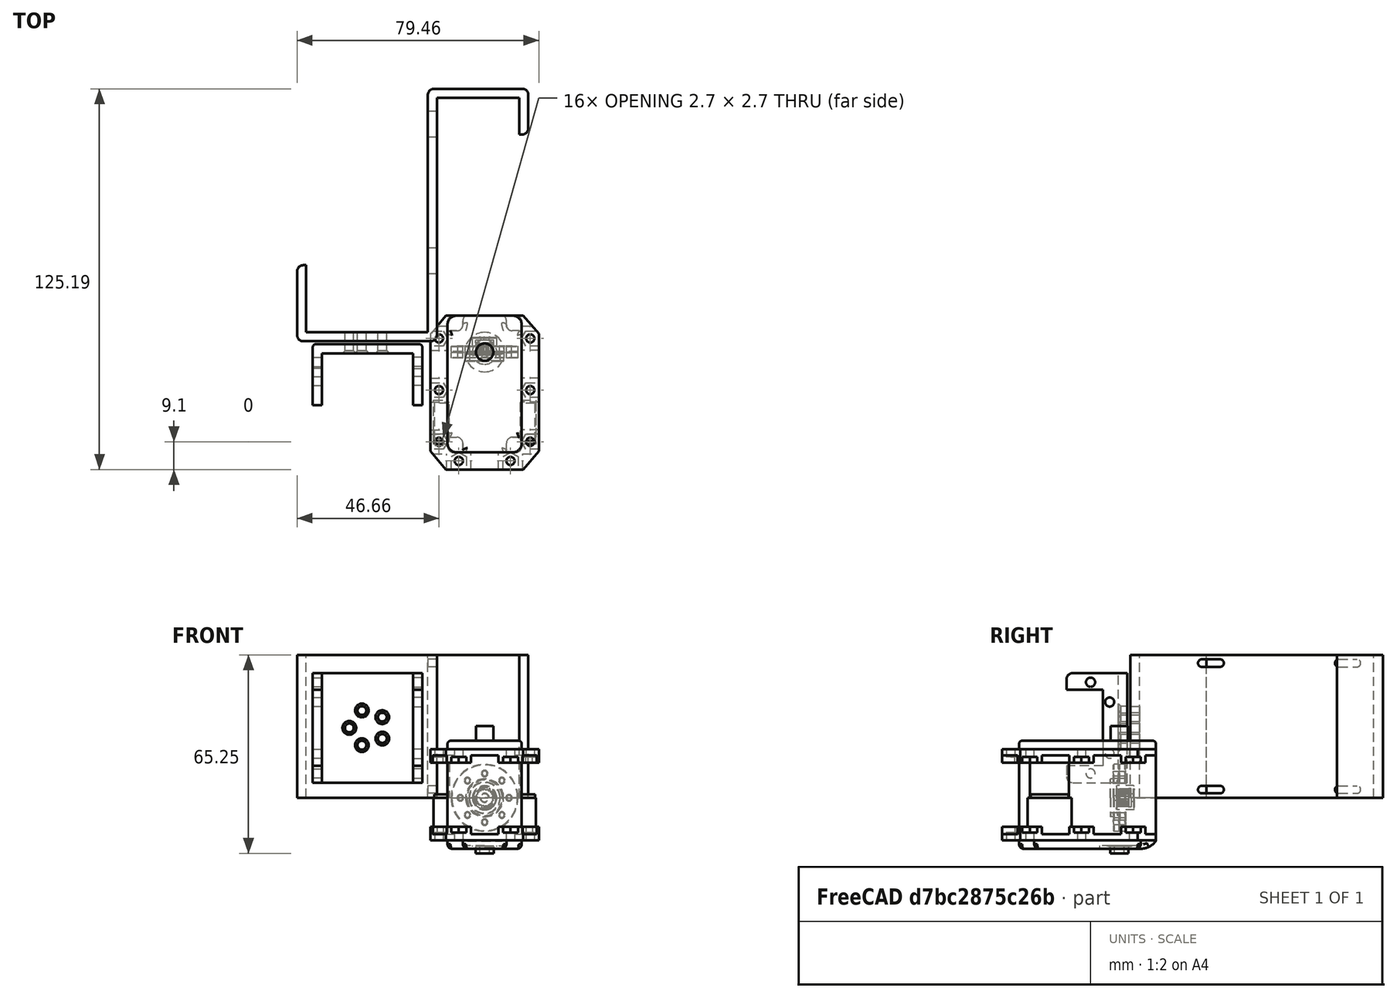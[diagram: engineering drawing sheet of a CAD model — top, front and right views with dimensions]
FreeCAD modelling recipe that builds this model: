
FCSTD DOCUMENT  (FreeCAD 1.1R20260414 (Git shallow))
Label: test2
License: All rights reserved
LicenseURL: https://en.wikipedia.org/wiki/All_rights_reserved
objects: App::Link×7, App::FeaturePython×7, App::Point×6, Sketcher::SketchObject×6, Part::Feature×5, PartDesign::Pad×3, PartDesign::Fillet×3, App::Part×3, PartDesign::Hole×2, PartDesign::Body×2, PartDesign::ShapeBinder×1, PartDesign::Mirrored×1, PartDesign::PolarPattern×1, Assembly::JointGroup×1, Assembly::AssemblyObject×1, PartDesign::Pocket×1, PartDesign::LinearPattern×1
note: 53 computed .brp shape members not serialized (recipe doc carries the construction recipe); baked Part::Feature solids carry a one-line shape summary decoded from their .brp
EXTERNAL_REF file=../test4/test4.FCStd obj=Body001
EXTERNAL_REF file=../test4/test4.FCStd obj=Body
EXTERNAL_REF file=../test4/test4.FCStd obj=ASM0001_ASM

FEATURE [App::Point] Origin001
  Role = Origin
FEATURE [Sketcher::SketchObject] Sketch
  ArcFitTolerance = 1e-06
  AttachmentSupport = -> [Origin]
  ExternalTypes = [0]
  FullyConstrained = true
  MakeInternals = false
  MapMode = 5
  _ExternalGeoVersion = 1
  sketch-geometry (12):
    g0: LineSegment StartX=-18.66 StartY=86.59 StartZ=0 EndX=-18.66 EndY=6.59 EndZ=0
    g1: LineSegment StartX=-61.66 StartY=3.59 StartZ=0 EndX=-61.66 EndY=28.59 EndZ=0
    g2: LineSegment StartX=-61.66 StartY=28.59 StartZ=0 EndX=-58.66 EndY=28.59 EndZ=0
    g3: LineSegment StartX=-58.66 StartY=28.59 StartZ=0 EndX=-58.66 EndY=6.59 EndZ=0
    g4: LineSegment StartX=-58.66 StartY=6.59 StartZ=0 EndX=-18.66 EndY=6.59 EndZ=0
    g5: LineSegment StartX=-15.66 StartY=83.59 StartZ=0 EndX=-15.66 EndY=3.59 EndZ=0
    g6: LineSegment StartX=-15.66 StartY=3.59 StartZ=0 EndX=-61.66 EndY=3.59 EndZ=0
    g7: LineSegment StartX=-15.66 StartY=83.59 StartZ=0 EndX=11.34 EndY=83.59 EndZ=0
    g8: LineSegment StartX=11.34 StartY=83.59 StartZ=0 EndX=11.34 EndY=71.59 EndZ=0
    g9: LineSegment StartX=11.34 StartY=71.59 StartZ=0 EndX=14.34 EndY=71.59 EndZ=0
    g10: LineSegment StartX=14.34 StartY=71.59 StartZ=0 EndX=14.34 EndY=86.59 EndZ=0
    g11: LineSegment StartX=14.34 StartY=86.59 StartZ=0 EndX=-18.66 EndY=86.59 EndZ=0
  constraints (36):
    c: Coincident(g1,g2)
    c: Coincident(g2,g3)
    c: Coincident(g3,g4)
    c: Coincident(g4,g0)
    c: Distance(g2,g2) = 3
    c: Vertical(g5)
    c: Coincident(g5,g6)
    c: Coincident(g6,g1)
    c: Perpendicular(g4,g3)
    c: Horizontal(g4)
    c: Horizontal(g6)
    c: Vertical(g1)
    c: Vertical(g0)
    c: Horizontal(g2)
    c: Distance(g6,g4) = 3
    c: Distance(g5,g0) = 3
    c: DistanceX(g4,g4) = 40
    c: Distance(g1,g1) = 25
    c: Distance(g-2,g5) = 15.66
    c: Distance(g-1,g6) = 3.59
    c: DistanceY(g0,g0) = 80
    c: Coincident(g5,g7)
    c: Horizontal(g7)
    c: Coincident(g7,g8)
    c: Vertical(g8)
    c: Coincident(g8,g9)
    c: Horizontal(g9)
    c: Coincident(g9,g10)
    c: Vertical(g10)
    c: Coincident(g10,g11)
    c: Coincident(g11,g0)
    c: Equal(g9,g2)
    c: Horizontal(g11)
    c: Distance(g11,g7) = 3
    c: Distance(g7,g7) = 27
    c: DistanceY(g10,g10) = 15
FEATURE [PartDesign::Pad] Pad
  Direction = (0,0,1)
  Length = 47
  Length2 = 10
  Profile = -> Sketch
  ReferenceAxis = -> Sketch [N_Axis]
  Refine = true
  SideType = 0
  Suppressed = false
  Type = 0
  Type2 = 0
FEATURE [Sketcher::SketchObject] Sketch001
  ArcFitTolerance = 1e-06
  ExternalTypes = [0]
  FullyConstrained = true
  MakeInternals = false
  MapMode = 5
  Placement = pos=(-15.66,0,0) rot=(0.57735,0.57735,0.57735;2.0944rad)
  _ExternalGeoVersion = 1
  sketch-geometry (8):
    g0: ArcOfCircle CenterX=72.09 CenterY=2.7 CenterZ=0 NormalX=0 NormalY=0 NormalZ=1 AngleXU=0 Radius=1.25 StartAngle=1.5708 EndAngle=4.71239
    g1: ArcOfCircle CenterX=78.09 CenterY=2.7 CenterZ=0 NormalX=0 NormalY=0 NormalZ=1 AngleXU=0 Radius=1.25 StartAngle=4.71239 EndAngle=7.85398
    g2: LineSegment StartX=72.09 StartY=3.95 StartZ=0 EndX=78.09 EndY=3.95 EndZ=0
    g3: LineSegment StartX=72.09 StartY=1.45 StartZ=0 EndX=78.09 EndY=1.45 EndZ=0
    g4: ArcOfCircle CenterX=27.09 CenterY=2.7 CenterZ=0 NormalX=0 NormalY=0 NormalZ=1 AngleXU=0 Radius=1.25 StartAngle=1.5708 EndAngle=4.71239
    g5: ArcOfCircle CenterX=33.09 CenterY=2.7 CenterZ=0 NormalX=0 NormalY=0 NormalZ=1 AngleXU=0 Radius=1.25 StartAngle=4.71239 EndAngle=7.85398
    g6: LineSegment StartX=27.09 StartY=3.95 StartZ=0 EndX=33.09 EndY=3.95 EndZ=0
    g7: LineSegment StartX=27.09 StartY=1.45 StartZ=0 EndX=33.09 EndY=1.45 EndZ=0
  constraints (20):
    c: Tangent(g0,g2) = 1.5708
    c: Tangent(g0,g3) = -1.5708
    c: Tangent(g1,g2) = 1.5708
    c: Tangent(g1,g3) = -1.5708
    c: Equal(g0,g1)
    c: Distance(g0,g1) = 6
    c: Radius(g0) = 1.25
    c: Horizontal(g2)
    c: Distance(g1,g-1) = 2.7
    c: DistanceX(g-1,g1) = 78.09
    c: Tangent(g4,g6) = 1.5708
    c: Tangent(g4,g7) = -1.5708
    c: Tangent(g5,g6) = 1.5708
    c: Tangent(g5,g7) = -1.5708
    c: Equal(g4,g5)
    c: Distance(g4,g5) = 6
    c: Radius(g4) = 1.25
    c: Horizontal(g6)
    c: DistanceX(g5,g1) = 45
    c: Distance(g5,g-1) = 2.7
FEATURE [App::Point] Origin003
  Role = Origin
FEATURE [App::Point] Origin005  label="Origin006"
  Role = Origin
FEATURE [App::Link] Body003
  LinkPlacement = pos=(-38.5,-38.01,23) rot=(-0.707107,0,0.707107;3.14159rad)
  LinkedObject = -> Body001
  Placement = pos=(-38.5,-38.01,23) rot=(-0.707107,0,0.707107;3.14159rad)
FEATURE [PartDesign::ShapeBinder] CopyPart__Feature
  TraceSupport = false
FEATURE [Sketcher::SketchObject] Sketch002
  ArcFitTolerance = 1e-06
  AttachmentSupport = -> [CopyPart__Feature]
  ExternalTypes = [0]
  FullyConstrained = true
  MakeInternals = false
  MapMode = 5
  Placement = pos=(0,-38.6,0) rot=(1,0,0;1.5708rad)
  _ExternalGeoVersion = 1
  sketch-geometry (5):
    g0: LineSegment StartX=-18 StartY=-15 StartZ=0 EndX=18 EndY=-15 EndZ=0
    g1: LineSegment StartX=18 StartY=-15 StartZ=0 EndX=18 EndY=15 EndZ=0
    g2: LineSegment StartX=18 StartY=15 StartZ=0 EndX=-18 EndY=15 EndZ=0
    g3: LineSegment StartX=-18 StartY=15 StartZ=0 EndX=-18 EndY=-15 EndZ=0
    g4: GeomPoint [constr] X=0 Y=0 Z=0
  constraints (12):
    c: Coincident(g0,g1)
    c: Coincident(g1,g2)
    c: Coincident(g2,g3)
    c: Coincident(g3,g0)
    c: Horizontal(g0)
    c: Horizontal(g2)
    c: Vertical(g1)
    c: Vertical(g3)
    c: Symmetric(g2,g0,g4)
    c: Distance(g1,g3) = 36
    c: Distance(g0,g2) = 30
    c: Coincident(g4,g-1)
FEATURE [PartDesign::Pad] Pad001
  Direction = (0,-1,2e-16)
  Length = 3
  Length2 = 10
  Profile = -> Sketch002
  ReferenceAxis = -> Sketch002 [N_Axis]
  Refine = true
  SideType = 0
  Suppressed = false
  Type = 0
  Type2 = 0
FEATURE [Sketcher::SketchObject] Sketch003
  ArcFitTolerance = 1e-06
  AttachmentSupport = -> [Pad001]
  ExternalTypes = [0]
  FullyConstrained = true
  MakeInternals = false
  MapMode = 5
  Placement = pos=(0,3.3e-15,15) rot=(0,0,1;0rad)
  _ExternalGeoVersion = 1
  sketch-geometry (12):
    g0: LineSegment StartX=-18 StartY=-21.6 StartZ=0 EndX=-12.5 EndY=-21.6 EndZ=0
    g1: LineSegment StartX=-12.5 StartY=-21.6 StartZ=0 EndX=-12.5 EndY=-33.6 EndZ=0
    g2: LineSegment StartX=-12.5 StartY=-33.6 StartZ=0 EndX=12.5 EndY=-33.6 EndZ=0
    g3: LineSegment StartX=12.5 StartY=-33.6 StartZ=0 EndX=12.5 EndY=-21.6 EndZ=0
    g4: LineSegment StartX=12.5 StartY=-21.6 StartZ=0 EndX=18 EndY=-21.6 EndZ=0
    g5: LineSegment StartX=18 StartY=-21.6 StartZ=0 EndX=18 EndY=-41.6 EndZ=0
    g6: LineSegment StartX=18 StartY=-41.6 StartZ=0 EndX=-18 EndY=-41.6 EndZ=0
    g7: LineSegment StartX=-18 StartY=-41.6 StartZ=0 EndX=-18 EndY=-21.6 EndZ=0
    g8: Circle CenterX=-15 CenterY=-29.5 CenterZ=0 NormalX=0 NormalY=0 NormalZ=1 AngleXU=0 Radius=1.5
    g9: Circle CenterX=-8.5 CenterY=-35.8 CenterZ=0 NormalX=0 NormalY=0 NormalZ=1 AngleXU=0 Radius=1.5
    g10: Circle CenterX=8.5 CenterY=-35.8 CenterZ=0 NormalX=0 NormalY=0 NormalZ=1 AngleXU=0 Radius=1.5
    g11: Circle CenterX=15 CenterY=-29.5 CenterZ=0 NormalX=0 NormalY=0 NormalZ=1 AngleXU=0 Radius=1.5
  constraints (36):
    c: Horizontal(g0)
    c: Coincident(g0,g1)
    c: Vertical(g1)
    c: Coincident(g1,g2)
    c: Horizontal(g2)
    c: Coincident(g2,g3)
    c: Vertical(g3)
    c: Coincident(g3,g4)
    c: Horizontal(g4)
    c: Coincident(g4,g5)
    c: Vertical(g5)
    c: Coincident(g5,g6)
    c: Horizontal(g6)
    c: Coincident(g6,g7)
    c: Coincident(g7,g0)
    c: Vertical(g7)
    c: DistanceX(g6,g6) = 36
    c: DistanceY(g7,g7) = 20
    c: Distance(g3,g1) = 25
    c: Equal(g0,g4)
    c: Equal(g3,g1)
    c: Distance(g-1,g6) = 41.6
    c: Distance(g-2,g7) = 18
    c: Distance(g6,g2) = 8
    c: Diameter(g8) = 3
    c: Equal(g8,g9)
    c: Equal(g9,g10)
    c: Equal(g10,g11)
    c: Distance(g8,g7) = 3
    c: Distance(g9,g6) = 5.8
    c: Distance(g9,g7) = 9.5
    c: Distance(g10,g5) = 9.5
    c: Distance(g10,g6) = 5.8
    c: Distance(g11,g5) = 3
    c: Distance(g8,g0) = 7.9
    c: Distance(g11,g4) = 7.9
FEATURE [PartDesign::Pad] Pad002
  BaseFeature = -> Pad001
  Direction = (0,0,1)
  Length = 3
  Length2 = 10
  Profile = -> Sketch003
  ReferenceAxis = -> Sketch003 [N_Axis]
  Refine = true
  SideType = 0
  Suppressed = false
  Type = 0
  Type2 = 0
FEATURE [PartDesign::Mirrored] Mirrored
  BaseFeature = -> Pad002
  MirrorPlane = -> XY_Plane001
  Originals = -> [Pad002]
  Refine = true
  Suppressed = false
  TransformMode = 0
FEATURE [PartDesign::Fillet] Fillet001
  Base = -> Mirrored [Edge60,Edge47,Edge36,Edge27]
  BaseFeature = -> Mirrored
  Radius = 2
  Refine = true
  SupportTransform = false
  Suppressed = false
  UseAllEdges = false
FEATURE [PartDesign::Fillet] Fillet002
  Base = -> Fillet001 [Edge51,Edge56]
  BaseFeature = -> Fillet001
  Radius = 1
  Refine = true
  SupportTransform = false
  Suppressed = false
  UseAllEdges = false
FEATURE [Sketcher::SketchObject] Sketch004
  ArcFitTolerance = 1e-06
  AttachmentSupport = -> [Fillet002]
  ExternalTypes = [0]
  FullyConstrained = true
  MakeInternals = false
  MapMode = 5
  Placement = pos=(0,-38.6,0) rot=(0,0.707107,0.707107;3.14159rad)
  _ExternalGeoVersion = 1
  sketch-geometry (1):
    g0: Circle CenterX=0 CenterY=6 CenterZ=0 NormalX=0 NormalY=0 NormalZ=1 AngleXU=0 Radius=1.25
  constraints (3):
    c: Diameter(g0) = 2.5
    c: PointOnObject(g0,g-2)
    c: Distance(g0,g-1) = 6
FEATURE [PartDesign::Hole] Hole
  BaseFeature = -> Fillet002
  BaseProfileType = 7
  CustomThreadClearance = 0
  Depth = 5
  DepthType = 0
  Diameter = 2.9
  DrillForDepth = false
  DrillPoint = 1
  DrillPointAngle = 118
  HoleCutCountersinkAngle = 90
  HoleCutCustomValues = false
  HoleCutDepth = 2.65
  HoleCutDiameter = 5.3
  HoleCutType = 7
  ModelThread = false
  Profile = -> Sketch004
  Refine = true
  Suppressed = false
  Tapered = false
  TaperedAngle = 90
  ThreadClass = 0
  ThreadDepth = 5
  ThreadDepthType = 0
  ThreadDiameter = 2.5
  ThreadDirection = 0
  ThreadFit = 0
  ThreadSize = 8
  ThreadType = 1
  Threaded = false
  UseCustomThreadClearance = false
FEATURE [PartDesign::PolarPattern] PolarPattern
  Angle = 360
  Axis = -> Sketch004 [N_Axis]
  BaseFeature = -> Hole
  Mode = 0
  Occurrences = 5
  Offset = 120
  Originals = -> [Hole]
  Refine = true
  SpacingPattern = [0]
  Spacings = [-1,-1,-1,-1]
  Suppressed = false
  TransformMode = 0
FEATURE [PartDesign::Body] Body001
  AllowCompound = true
  Group = -> [CopyPart__Feature,Sketch002,Pad001,Sketch003,Pad002,Mirrored,Fillet001,Fillet002,Sketch004,Hole,PolarPattern]
  Origin = -> Origin002
  Placement = pos=(-38.5,-39,23) rot=(0.707107,0,-0.707107;3.14159rad)
  Tip = -> PolarPattern
FEATURE [App::Link] Body004
  LinkedObject = -> Body
FEATURE [App::FeaturePython] GroundedJoint  label="GroundedJoint001"  # Assembly grounded joint (typed FeaturePython)
  ObjectToGround = -> Body004
FEATURE [App::FeaturePython] Joint  label="Fixed015"  # Assembly joint (typed FeaturePython)
  Angle = 0
  AngleMax = 0
  AngleMin = 0
  Detach1 = false
  Detach2 = false
  Distance = 0
  Distance2 = 0
  EnableAngleMax = false
  EnableAngleMin = false
  EnableLengthMax = false
  EnableLengthMin = false
  JointType = 0 (Fixed)
  LengthMax = 0
  LengthMin = 0
  Offset2 = pos=(0,0,0) rot=(0,0,1;1.5708rad)
  Placement1 = pos=(-44.5,3.59,23) rot=(0,-0.707107,0.707107;3.14159rad)
  Placement2 = pos=(3.6e-15,-41.6,6) rot=(0.57735,-0.57735,0.57735;2.0944rad)
  Reference1 = -> Body004 [Edge68,Edge68]
  Reference2 = -> Body003 [Edge32,Edge32]
  Suppressed = false
FEATURE [App::Point] Origin006  label="Origin008"
  Role = Origin
FEATURE [Part::Feature] Part__Feature  label="DC07_00A_DUMMY_NONE"
  Placement = pos=(0,0,1) rot=(0,0,1;0rad)
  shape: bbox 35.6 x 51.12 x 41.85 mm, 333 faces (baked)
FEATURE [App::Point] Origin008  label="Origin010"
  Role = Origin
FEATURE [Part::Feature] Part__Feature001  label="SOLID001"
  shape: bbox 22 x 3.05 x 22 mm, 56 faces (baked)
FEATURE [Part::Feature] Part__Feature002  label="COMPOUND001"
  shape: bbox 18 x 1.95 x 18 mm, 16 faces, 0 solids (baked)
FEATURE [App::Part] HN07_I_02
  Group = -> [Part__Feature001,Part__Feature002]
  Origin = -> Origin009
  Placement = pos=(2e-16,0,-19.15) rot=(-0.672416,0.523382,-0.523382;1.95765rad)
FEATURE [App::Point] Origin010  label="Origin012"
  Role = Origin
FEATURE [Part::Feature] Part__Feature003  label="SOLID"
  shape: bbox 22 x 5.851 x 22 mm, 149 faces (baked)
FEATURE [Part::Feature] Part__Feature004  label="COMPOUND"
  shape: bbox 18 x 1.95 x 18 mm, 16 faces, 0 solids (baked)
FEATURE [App::Part] HN07_N_02
  Group = -> [Part__Feature003,Part__Feature004]
  Origin = -> Origin011
  Placement = pos=(0,0,19.3) rot=(0.57735,0.57735,0.57735;2.0944rad)
FEATURE [App::Part] Unnamed  label="mx28"
  Group = -> [Part__Feature,HN07_I_02,HN07_N_02]
  Origin = -> Origin007
FEATURE [App::Link] mx28  label="mx001"
  LinkPlacement = pos=(-37.5,-38.01,23) rot=(-0.707107,0,0.707107;3.14159rad)
  LinkedObject = -> Unnamed
  Placement = pos=(-37.5,-38.01,23) rot=(-0.707107,0,0.707107;3.14159rad)
FEATURE [App::FeaturePython] Joint001  label="Fixed017"  # Assembly joint (typed FeaturePython)
  Angle = 0
  AngleMax = 0
  AngleMin = 0
  Detach1 = false
  Detach2 = false
  Distance = 0
  Distance2 = 0
  EnableAngleMax = false
  EnableAngleMin = false
  EnableLengthMax = false
  EnableLengthMin = false
  JointType = 0 (Fixed)
  LengthMax = 0
  LengthMin = 0
  Offset2 = pos=(0,0,-1.5) rot=(0,0,1;0rad)
  Placement1 = pos=(8.5,-35.8,15) rot=(1,0,0;3.14159rad)
  Placement2 = pos=(8.5,-35.8,15) rot=(0,0,1;0rad)
  Reference1 = -> mx28 [Part__Feature.Edge697,Part__Feature.Edge697]
  Reference2 = -> Body003 [Face21,Face21]
  Suppressed = false
FEATURE [App::Link] Body005
  LinkPlacement = pos=(-30.115,-30.5656,31.2547) rot=(-0.706989,-0.018235,0.706989;3.10513rad)
  LinkedObject = -> <external ../test4/test4.FCStd>#Body001
  Placement = pos=(-30.115,-30.5656,31.2547) rot=(-0.706989,-0.018235,0.706989;3.10513rad)
FEATURE [App::FeaturePython] Joint002  label="Revolute018"  # Assembly joint (typed FeaturePython)
  Angle = 0
  AngleMax = 0
  AngleMin = 0
  Detach1 = false
  Detach2 = false
  Distance = 0
  Distance2 = 0
  EnableAngleMax = false
  EnableAngleMin = false
  EnableLengthMax = false
  EnableLengthMin = false
  JointType = 1 (Revolute)
  LengthMax = 0
  LengthMin = 0
  Offset2 = pos=(0,0,2.5) rot=(0,0,1;0rad)
  Placement1 = pos=(0,4.65,0) rot=(0,-0.707107,0.707107;3.14159rad)
  Placement2 = pos=(7.86,7.86,31.335) rot=(0,0,1;0rad)
  Reference1 = -> mx28 [HN07_N_02.Part__Feature003.Face53,HN07_N_02.Part__Feature003.Edge4]
  Reference2 = -> Body005 [Edge45,Edge45]
  Suppressed = false
FEATURE [App::Link] Body006
  LinkPlacement = pos=(-16.8936,-106.981,69.1522) rot=(0.706989,0.018235,-0.706989;3.17806rad)
  LinkedObject = -> <external ../test4/test4.FCStd>#Body
  Placement = pos=(-16.8936,-106.981,69.1522) rot=(0.706989,0.018235,-0.706989;3.17806rad)
FEATURE [App::Link] ASM0001_ASM
  LinkPlacement = pos=(-16.5936,-105.125,33.2001) rot=(0.706989,-0.018235,0.706989;3.17806rad)
  LinkedObject = -> <external ../test4/test4.FCStd>#ASM0001_ASM
  Placement = pos=(-16.5936,-105.125,33.2001) rot=(0.706989,-0.018235,0.706989;3.17806rad)
FEATURE [App::Link] ASM0001_ASM001
  LinkPlacement = pos=(-16.5936,-106.981,69.1522) rot=(0.706989,-0.018235,0.706989;3.17806rad)
  LinkedObject = -> <external ../test4/test4.FCStd>#ASM0001_ASM
  Placement = pos=(-16.5936,-106.981,69.1522) rot=(0.706989,-0.018235,0.706989;3.17806rad)
FEATURE [App::FeaturePython] Joint003  label="Fixed021"  # Assembly joint (typed FeaturePython)
  Angle = 0
  AngleMax = 0
  AngleMin = 0
  Detach1 = false
  Detach2 = false
  Distance = 0
  Distance2 = 0
  EnableAngleMax = false
  EnableAngleMin = false
  EnableLengthMax = false
  EnableLengthMin = false
  JointType = 0 (Fixed)
  LengthMax = 0
  LengthMin = 0
  Placement1 = pos=(10.2136,32.86,3.77861) rot=(0.57735,0.57735,0.57735;4.18879rad)
  Placement2 = pos=(52,-41.5,17) rot=(0.57735,0.57735,0.57735;4.18879rad)
  Reference1 = -> Body005 [Face9,Vertex51]
  Reference2 = -> Body006 [Face28,Edge6]
  Suppressed = false
FEATURE [App::FeaturePython] Joint004  label="Fixed022"  # Assembly joint (typed FeaturePython)
  Angle = 0
  AngleMax = 0
  AngleMin = 0
  Detach1 = false
  Detach2 = false
  Distance = 0
  Distance2 = 0
  EnableAngleMax = false
  EnableAngleMin = false
  EnableLengthMax = false
  EnableLengthMin = false
  JointType = 0 (Fixed)
  LengthMax = 0
  LengthMin = 0
  Offset2 = pos=(0,0,-0.2) rot=(0,0,-1;1.5708rad)
  Placement1 = pos=(13.5,-30.5,16) rot=(0,0,1;1.5708rad)
  Placement2 = pos=(-13.5,-30.5,-16.3) rot=(-0.707107,-0.707107,0;3.14159rad)
  Reference1 = -> ASM0001_ASM001 [ASM0002_ASM.Part__Feature.Edge804,ASM0002_ASM.Part__Feature.Edge804]
  Reference2 = -> Body006 [Edge110,Edge110]
  Suppressed = false
FEATURE [App::FeaturePython] Joint005  label="Fixed023"  # Assembly joint (typed FeaturePython)
  Angle = 0
  AngleMax = 0
  AngleMin = 0
  Detach1 = false
  Detach2 = false
  Distance = 0
  Distance2 = 0
  EnableAngleMax = false
  EnableAngleMin = false
  EnableLengthMax = false
  EnableLengthMin = false
  JointType = 0 (Fixed)
  LengthMax = 0
  LengthMin = 0
  Offset2 = pos=(0,0,-0.2) rot=(0,0,1;1.5708rad)
  Placement1 = pos=(-13.5,-30.5,16) rot=(0,0,-1;1.5708rad)
  Placement2 = pos=(49.5,-30.5,-16.3) rot=(-0.707107,0.707107,0;3.14159rad)
  Reference1 = -> ASM0001_ASM [ASM0002_ASM.Part__Feature.Edge809,ASM0002_ASM.Part__Feature.Edge809]
  Reference2 = -> Body006 [Edge104,Edge104]
  Suppressed = false
FEATURE [Assembly::JointGroup] Joints
  Group = -> [GroundedJoint,Joint,Joint001,Joint002,Joint003,Joint004,Joint005]
FEATURE [Assembly::AssemblyObject] Assembly
  Group = -> [Joints,Body003,Body004,GroundedJoint,Joint,mx28,Joint001,Body005,Joint002,Body006,ASM0001_ASM,ASM0001_ASM001,Joint003,Joint004,Joint005]
  Origin = -> Origin004
  Type = Assembly
FEATURE [PartDesign::Fillet] Fillet
  Base = -> Pad [Edge26,Edge29,Edge32,Edge8,Edge11,Edge14]
  BaseFeature = -> Pad
  Radius = 2
  Refine = true
  SupportTransform = false
  Suppressed = false
  UseAllEdges = false
FEATURE [PartDesign::Pocket] Pocket
  BaseFeature = -> Fillet
  Direction = (-1,0,0)
  Length = 5
  Length2 = 5
  Profile = -> Sketch001
  ReferenceAxis = -> Sketch001 [N_Axis]
  Refine = true
  SideType = 0
  Suppressed = false
  Type = 0
  Type2 = 0
FEATURE [PartDesign::LinearPattern] LinearPattern
  BaseFeature = -> Pocket
  Direction = -> Sketch001 [V_Axis]
  Direction2 = -> Sketch001 [V_Axis]
  Length = 41.6
  Length2 = 100
  Mode = 0
  Mode2 = 0
  Occurrences = 2
  Occurrences2 = 1
  Offset = 41.6
  Offset2 = 100
  Originals = -> [Pocket]
  Refine = true
  Reversed2 = false
  SpacingPattern = [0]
  SpacingPattern2 = [0]
  Spacings = [-1]
  Suppressed = false
  TransformMode = 0
FEATURE [Sketcher::SketchObject] Sketch005
  ArcFitTolerance = 1e-06
  AttachmentSupport = -> [LinearPattern]
  ExternalTypes = [0]
  FullyConstrained = true
  MakeInternals = false
  Placement = pos=(0,3.59,0) rot=(1,0,0;1.5708rad)
  _ExternalGeoVersion = 1
  sketch-geometry (5):
    g0: Circle CenterX=-40.37 CenterY=17.3 CenterZ=0 NormalX=0 NormalY=0 NormalZ=1 AngleXU=0 Radius=1.25
    g1: Circle CenterX=-44.5 CenterY=23 CenterZ=0 NormalX=0 NormalY=0 NormalZ=1 AngleXU=0 Radius=1.25
    g2: Circle CenterX=-40.36 CenterY=28.7 CenterZ=0 NormalX=0 NormalY=0 NormalZ=1 AngleXU=0 Radius=1.25
    g3: Circle CenterX=-33.65 CenterY=26.55 CenterZ=0 NormalX=0 NormalY=0 NormalZ=1 AngleXU=0 Radius=1.25
    g4: Circle CenterX=-33.65 CenterY=19.5 CenterZ=0 NormalX=0 NormalY=0 NormalZ=1 AngleXU=0 Radius=1.25
  constraints (15):
    c: Diameter(g0) = 2.5
    c: Distance(g0,g-1) = 17.3
    c: Distance(g0,g-2) = 40.37
    c: Equal(g1,g0)
    c: Distance(g1,g-1) = 23
    c: DistanceX(g1,g-1) = 44.5
    c: Equal(g2,g1)
    c: Equal(g3,g2)
    c: Equal(g4,g3)
    c: Distance(g2,g-1) = 28.7
    c: Distance(g2,g-2) = 40.36
    c: Distance(g3,g-2) = 33.65
    c: Distance(g3,g-1) = 26.55
    c: Distance(g4,g-2) = 33.65
    c: DistanceY(g-1,g4) = 19.5
FEATURE [PartDesign::Hole] Hole001
  BaseFeature = -> LinearPattern
  BaseProfileType = 7
  CustomThreadClearance = 0
  Depth = 5
  DepthType = 0
  Diameter = 2.9
  DrillForDepth = false
  DrillPoint = 1
  DrillPointAngle = 118
  HoleCutCountersinkAngle = 90
  HoleCutCustomValues = false
  HoleCutDepth = 0
  HoleCutDiameter = 5.3
  HoleCutType = 0
  ModelThread = false
  Profile = -> Sketch005
  Refine = true
  Suppressed = false
  Tapered = false
  TaperedAngle = 90
  ThreadClass = 0
  ThreadDepth = 5
  ThreadDepthType = 0
  ThreadDiameter = 2.5
  ThreadDirection = 0
  ThreadFit = 0
  ThreadSize = 8
  ThreadType = 1
  Threaded = false
  UseCustomThreadClearance = false
FEATURE [PartDesign::Body] Body
  AllowCompound = true
  Group = -> [Sketch,Pad,Fillet,Sketch001,Pocket,LinearPattern,Sketch005,Hole001]
  Origin = -> Origin
  Tip = -> Hole001

RESOLVED EXTERNAL PARTS (link-assembly join: the EXTERNAL_REF files above that resolve inside this repo's crawl, each included once):
---- part ../test4/test4.FCStd = doc fcstd_3a8577a0ba73 ----
FCSTD DOCUMENT  (FreeCAD 1.1R20260414 (Git shallow))
Label: test4
License: All rights reserved
LicenseURL: https://en.wikipedia.org/wiki/All_rights_reserved
objects: Sketcher::SketchObject×26, Part::Feature×23, PartDesign::Pad×16, PartDesign::Hole×10, App::Point×8, PartDesign::Fillet×7, PartDesign::PolarPattern×5, App::Part×4, PartDesign::ShapeBinder×4, PartDesign::Body×4, PartDesign::Mirrored×3
note: 198 computed .brp shape members not serialized (recipe doc carries the construction recipe); baked Part::Feature solids carry a one-line shape summary decoded from their .brp

FEATURE [Part::Feature] Part__Feature  label="PRT0001"
  shape: bbox 32 x 50.5 x 38 mm, 671 faces (baked)
FEATURE [Part::Feature] Part__Feature001  label="PRT0002"
  Placement = pos=(0,0,-2) rot=(0,0,1;3.14159rad)
  shape: bbox 7.033 x 7.036 x 5.513 mm, 32 faces (baked)
FEATURE [Part::Feature] Part__Feature002  label="PRT0003"
  Placement = pos=(9.5,8.5,14.5) rot=(0,0.707107,0.707107;3.14159rad)
  shape: bbox 4.1 x 4.088 x 30.71 mm, 30 faces (baked)
FEATURE [Part::Feature] Part__Feature003  label="PRT0004"
  Placement = pos=(-9.5,8.5,14.5) rot=(0,0.707107,0.707107;3.14159rad)
  shape: bbox 4.1 x 4.088 x 30.71 mm, 30 faces (baked)
FEATURE [Part::Feature] Part__Feature004  label="PRT0005"
  Placement = pos=(10.5,-33,14.5) rot=(0,0.707107,0.707107;3.14159rad)
  shape: bbox 4.1 x 4.088 x 30.71 mm, 30 faces (baked)
FEATURE [Part::Feature] Part__Feature005  label="PRT0006"
  Placement = pos=(-10.5,-33,14.5) rot=(0,0.707107,0.707107;3.14159rad)
  shape: bbox 4.1 x 4.088 x 30.71 mm, 30 faces (baked)
FEATURE [Part::Feature] Part__Feature006  label="PRT0007"
  Placement = pos=(5.05,-15.19,-9.75) rot=(-1,0,0;1.5708rad)
  shape: bbox 9.902 x 4.902 x 9.405 mm, 93 faces (baked)
FEATURE [Part::Feature] Part__Feature007  label="PRT0008"
  Placement = pos=(-4.95,-15.19,-9.75) rot=(-1,0,0;1.5708rad)
  shape: bbox 9.902 x 4.902 x 9.405 mm, 93 faces (baked)
FEATURE [Part::Feature] Part__Feature008  label="PRT0009"
  Placement = pos=(0,0,-18.4) rot=(0,0.707107,0.707107;3.14159rad)
  shape: bbox 4.984 x 4.984 x 7 mm, 133 faces (baked)
FEATURE [Part::Feature] Part__Feature009  label="PRT0010"
  Placement = pos=(0,0,19.16) rot=(0,0,1;1.5708rad)
  shape: bbox 22 x 22 x 6.702 mm, 170 faces (baked)
FEATURE [Part::Feature] Part__Feature010  label="PRT0011"
  Placement = pos=(0,0,19.48) rot=(0,0.707107,0.707107;3.14159rad)
  shape: bbox 7.815 x 6.706 x 9.6 mm, 27 faces (baked)
FEATURE [App::Part] ASM0002_ASM
  Group = -> [Part__Feature,Part__Feature001,Part__Feature002,Part__Feature003,Part__Feature004,Part__Feature005,Part__Feature006,Part__Feature007,Part__Feature008,Part__Feature009,Part__Feature010]
  Origin = -> Origin
FEATURE [App::Point] Origin001
  Role = Origin
FEATURE [App::Part] ASM0001_ASM
  Group = -> [ASM0002_ASM]
  Origin = -> Origin002
  Placement = pos=(-5,-22,0) rot=(0,0,1;4.71239rad)
FEATURE [App::Point] Origin003
  Role = Origin
FEATURE [App::Point] Origin005  label="Origin006"
  Role = Origin
FEATURE [PartDesign::ShapeBinder] CopyPart__Feature
  TraceSupport = false
FEATURE [Sketcher::SketchObject] Sketch
  ArcFitTolerance = 1e-06
  AttachmentSupport = -> [CopyPart__Feature]
  ExternalTypes = [0]
  FullyConstrained = true
  MakeInternals = false
  MapMode = 5
  Placement = pos=(0,-38.5,0) rot=(1,0,0;1.5708rad)
  _ExternalGeoVersion = 1
  sketch-geometry (5):
    g0: LineSegment StartX=-44.42 StartY=-19 StartZ=0 EndX=69.58 EndY=-19 EndZ=0
    g1: LineSegment StartX=69.58 StartY=-19 StartZ=0 EndX=69.58 EndY=19 EndZ=0
    g2: LineSegment StartX=69.58 StartY=19 StartZ=0 EndX=-44.42 EndY=19 EndZ=0
    g3: LineSegment StartX=-44.42 StartY=19 StartZ=0 EndX=-44.42 EndY=-19 EndZ=0
    g4: GeomPoint [constr] X=12.58 Y=0 Z=0
  constraints (13):
    c: Coincident(g0,g1)
    c: Coincident(g1,g2)
    c: Coincident(g2,g3)
    c: Coincident(g3,g0)
    c: Horizontal(g0)
    c: Horizontal(g2)
    c: Vertical(g1)
    c: Vertical(g3)
    c: Symmetric(g2,g0,g4)
    c: Distance(g1,g3) = 114
    c: Distance(g0,g2) = 38
    c: PointOnObject(g4,g-1)
    c: Distance(g-2,g3) = 44.42
FEATURE [PartDesign::Pad] Pad
  Direction = (0,-1,0)
  Length = 5
  Length2 = 10
  Profile = -> Sketch
  ReferenceAxis = -> Sketch [N_Axis]
  Refine = true
  SideType = 0
  Suppressed = false
  Type = 0
  Type2 = 0
FEATURE [Sketcher::SketchObject] Sketch001
  ArcFitTolerance = 1e-06
  AttachmentSupport = -> [Pad]
  ExternalTypes = [0]
  FullyConstrained = true
  MakeInternals = false
  MapMode = 5
  Placement = pos=(0,-38.5,1.44e-14) rot=(0,0.707107,0.707107;3.14159rad)
  _ExternalGeoVersion = 1
  sketch-geometry (4):
    g0: LineSegment StartX=44.42 StartY=19 StartZ=0 EndX=-69.58 EndY=19 EndZ=0
    g1: LineSegment StartX=-69.58 StartY=19 StartZ=0 EndX=-69.58 EndY=15.5 EndZ=0
    g2: LineSegment StartX=-69.58 StartY=15.5 StartZ=0 EndX=44.42 EndY=15.5 EndZ=0
    g3: LineSegment StartX=44.42 StartY=15.5 StartZ=0 EndX=44.42 EndY=19 EndZ=0
  constraints (12):
    c: Coincident(g0,g1)
    c: Coincident(g1,g2)
    c: Coincident(g2,g3)
    c: Coincident(g3,g0)
    c: Horizontal(g0)
    c: Horizontal(g2)
    c: Vertical(g1)
    c: Vertical(g3)
    c: Distance(g-2,g3) = 44.42
    c: Distance(g2,g2) = 114
    c: Distance(g-1,g0) = 19
    c: Distance(g1,g1) = 3.5
FEATURE [PartDesign::Pad] Pad001
  BaseFeature = -> Pad
  Direction = (0,1,-2e-16)
  Length = 5
  Length2 = 10
  Profile = -> Sketch001
  ReferenceAxis = -> Sketch001 [N_Axis]
  Refine = true
  SideType = 0
  Suppressed = false
  Type = 0
  Type2 = 0
FEATURE [App::Point] Origin007  label="Origin009"
  Role = Origin
FEATURE [App::Point] Origin009  label="Origin011"
  Role = Origin
FEATURE [Part::Feature] Part__Feature011  label="PRT0012"
  shape: bbox 32 x 50.5 x 38 mm, 671 faces (baked)
FEATURE [Part::Feature] Part__Feature012  label="PRT0013"
  Placement = pos=(0,0,-2) rot=(0,0,1;3.14159rad)
  shape: bbox 7.033 x 7.036 x 5.513 mm, 32 faces (baked)
FEATURE [Part::Feature] Part__Feature013  label="PRT0014"
  Placement = pos=(9.5,8.5,14.5) rot=(0,0.707107,0.707107;3.14159rad)
  shape: bbox 4.1 x 4.088 x 30.71 mm, 30 faces (baked)
FEATURE [Part::Feature] Part__Feature014  label="PRT0015"
  Placement = pos=(-9.5,8.5,14.5) rot=(0,0.707107,0.707107;3.14159rad)
  shape: bbox 4.1 x 4.088 x 30.71 mm, 30 faces (baked)
FEATURE [Part::Feature] Part__Feature015  label="PRT0016"
  Placement = pos=(10.5,-33,14.5) rot=(0,0.707107,0.707107;3.14159rad)
  shape: bbox 4.1 x 4.088 x 30.71 mm, 30 faces (baked)
FEATURE [Part::Feature] Part__Feature016  label="PRT0017"
  Placement = pos=(-10.5,-33,14.5) rot=(0,0.707107,0.707107;3.14159rad)
  shape: bbox 4.1 x 4.088 x 30.71 mm, 30 faces (baked)
FEATURE [Part::Feature] Part__Feature017  label="PRT0018"
  Placement = pos=(5.05,-15.19,-9.75) rot=(-1,0,0;1.5708rad)
  shape: bbox 9.902 x 4.902 x 9.405 mm, 93 faces (baked)
FEATURE [Part::Feature] Part__Feature018  label="PRT0019"
  Placement = pos=(-4.95,-15.19,-9.75) rot=(-1,0,0;1.5708rad)
  shape: bbox 9.902 x 4.902 x 9.405 mm, 93 faces (baked)
FEATURE [Part::Feature] Part__Feature019  label="PRT0020"
  Placement = pos=(0,0,-18.4) rot=(0,0.707107,0.707107;3.14159rad)
  shape: bbox 4.984 x 4.984 x 7 mm, 133 faces (baked)
FEATURE [Part::Feature] Part__Feature020  label="PRT0021"
  Placement = pos=(0,0,19.16) rot=(0,0,1;1.5708rad)
  shape: bbox 22 x 22 x 6.702 mm, 170 faces (baked)
FEATURE [Part::Feature] Part__Feature021  label="PRT0022"
  Placement = pos=(0,0,19.48) rot=(0,0.707107,0.707107;3.14159rad)
  shape: bbox 7.815 x 6.706 x 9.6 mm, 27 faces (baked)
FEATURE [App::Part] ASM0002_ASM001
  Group = -> [Part__Feature011,Part__Feature012,Part__Feature013,Part__Feature014,Part__Feature015,Part__Feature016,Part__Feature017,Part__Feature018,Part__Feature019,Part__Feature020,Part__Feature021]
  Origin = -> Origin006
FEATURE [App::Part] ASM0001_ASM001
  Group = -> [ASM0002_ASM001]
  Origin = -> Origin008
  Placement = pos=(30,-22,0) rot=(0,0,1;1.5708rad)
FEATURE [PartDesign::ShapeBinder] CopyPart__Feature001
  Placement = pos=(7.86,7.86,9.485) rot=(0,0,1;0rad)
  TraceSupport = false
FEATURE [Sketcher::SketchObject] Sketch006
  ArcFitTolerance = 1e-06
  AttachmentSupport = -> [CopyPart__Feature001]
  ExternalTypes = [0]
  FullyConstrained = true
  MakeInternals = false
  MapMode = 5
  Placement = pos=(7.86,7.86,28.835) rot=(0,0,1;0rad)
  _ExternalGeoVersion = 1
  sketch-geometry (4):
    g0: LineSegment StartX=11.04 StartY=-2.7e-15 StartZ=0 EndX=11.04 EndY=25 EndZ=0
    g1: LineSegment StartX=11.04 StartY=25 StartZ=0 EndX=-10.96 EndY=25 EndZ=0
    g2: LineSegment StartX=-10.96 StartY=25 StartZ=0 EndX=-10.96 EndY=-2.62289e-05 EndZ=0
    g3: ArcOfCircle CenterX=0.04 CenterY=0 CenterZ=0 NormalX=0 NormalY=0 NormalZ=1 AngleXU=0 Radius=11 StartAngle=3.1416 EndAngle=6.28319
  constraints (12):
    c: Coincident(g0,g1)
    c: Coincident(g1,g2)
    c: Vertical(g0)
    c: Vertical(g2)
    c: Horizontal(g1)
    c: Distance(g0,g2) = 22
    c: Distance(g1,g0) = 25
    c: PointOnObject(g0,g-1)
    c: Tangent(g0,g3) = -1.5708
    c: Coincident(g3,g2)
    c: Radius(g3) = 11
    c: Distance(g3,g-2) = 10.96
FEATURE [PartDesign::Pad] Pad005
  Direction = (0,0,1)
  Length = 3
  Length2 = 10
  Placement = pos=(7.86,7.86,9.485) rot=(0,0,1;0rad)
  Profile = -> Sketch006
  ReferenceAxis = -> Sketch006 [N_Axis]
  Refine = true
  SideType = 0
  Suppressed = false
  Type = 0
  Type2 = 0
FEATURE [Sketcher::SketchObject] Sketch007
  ArcFitTolerance = 1e-06
  AttachmentSupport = -> [Pad005]
  ExternalTypes = [0]
  FullyConstrained = true
  MakeInternals = false
  MapMode = 5
  Placement = pos=(7.86,7.86,31.835) rot=(0,0,1;0rad)
  _ExternalGeoVersion = 1
  sketch-geometry (1):
    g0: Circle CenterX=0 CenterY=-7.8 CenterZ=0 NormalX=0 NormalY=0 NormalZ=1 AngleXU=0 Radius=1
  constraints (3):
    c: Diameter(g0) = 2
    c: PointOnObject(g0,g-2)
    c: Distance(g0,g-1) = 7.8
FEATURE [PartDesign::Hole] Hole001
  BaseFeature = -> Pad005
  BaseProfileType = 7
  CustomThreadClearance = 0
  Depth = 3
  DepthType = 0
  Diameter = 2.552
  DrillForDepth = false
  DrillPoint = 1
  DrillPointAngle = 118
  HoleCutCountersinkAngle = 90
  HoleCutCustomValues = false
  HoleCutDepth = 0
  HoleCutDiameter = 5.71648
  HoleCutType = 0
  ModelThread = false
  Placement = pos=(7.86,7.86,9.485) rot=(0,0,1;0rad)
  Profile = -> Sketch007
  Refine = true
  Suppressed = false
  Tapered = false
  TaperedAngle = 90
  ThreadClass = 0
  ThreadDepth = 3
  ThreadDepthType = 0
  ThreadDiameter = 2.2
  ThreadDirection = 0
  ThreadFit = 2
  ThreadSize = 7
  ThreadType = 1
  Threaded = false
  UseCustomThreadClearance = false
FEATURE [PartDesign::PolarPattern] PolarPattern
  Angle = 360
  Axis = -> Sketch007 [N_Axis]
  BaseFeature = -> Hole001
  Mode = 0
  Occurrences = 8
  Offset = 120
  Originals = -> [Hole001]
  Placement = pos=(7.86,7.86,9.485) rot=(0,0,1;0rad)
  Refine = true
  SpacingPattern = [0]
  Spacings = [-1,-1,-1,-1,-1,-1,-1]
  Suppressed = false
  TransformMode = 0
FEATURE [Sketcher::SketchObject] Sketch008
  ArcFitTolerance = 1e-06
  AttachmentSupport = -> [PolarPattern]
  ExternalTypes = [0]
  FullyConstrained = true
  MakeInternals = false
  MapMode = 5
  Placement = pos=(7.86,7.86,31.835) rot=(0,0,1;0rad)
  _ExternalGeoVersion = 1
  sketch-geometry (1):
    g0: Circle CenterX=0 CenterY=0 CenterZ=0 NormalX=0 NormalY=0 NormalZ=1 AngleXU=0 Radius=4
  constraints (2):
    c: Diameter(g0) = 8
    c: Coincident(g0,g-1)
FEATURE [PartDesign::Hole] Hole002
  BaseFeature = -> PolarPattern
  BaseProfileType = 7
  CustomThreadClearance = 0
  Depth = 3
  DepthType = 0
  Diameter = 6
  DrillForDepth = false
  DrillPoint = 1
  DrillPointAngle = 118
  HoleCutCountersinkAngle = 90
  HoleCutCustomValues = false
  HoleCutDepth = 0
  HoleCutDiameter = 0
  HoleCutType = 0
  ModelThread = false
  Placement = pos=(7.86,7.86,9.485) rot=(0,0,1;0rad)
  Profile = -> Sketch008
  Refine = true
  Suppressed = false
  Tapered = false
  TaperedAngle = 90
  ThreadClass = 0
  ThreadDepth = 3
  ThreadDepthType = 0
  ThreadDiameter = 6
  ThreadDirection = 0
  ThreadFit = 0
  ThreadSize = 0
  ThreadType = 0
  Threaded = false
  UseCustomThreadClearance = false
FEATURE [Sketcher::SketchObject] Sketch009
  ArcFitTolerance = 1e-06
  AttachmentSupport = -> [Hole002]
  ExternalTypes = [0]
  FullyConstrained = true
  MakeInternals = false
  MapMode = 5
  Placement = pos=(7.86,7.86,28.835) rot=(1,0,0;3.14159rad)
  _ExternalGeoVersion = 1
  sketch-geometry (4):
    g0: LineSegment StartX=11.04 StartY=-25 StartZ=0 EndX=11.04 EndY=-22 EndZ=0
    g1: LineSegment StartX=11.04 StartY=-22 StartZ=0 EndX=-10.96 EndY=-22 EndZ=0
    g2: LineSegment StartX=-10.96 StartY=-22 StartZ=0 EndX=-10.96 EndY=-25 EndZ=0
    g3: LineSegment StartX=-10.96 StartY=-25 StartZ=0 EndX=11.04 EndY=-25 EndZ=0
  constraints (12):
    c: Coincident(g0,g1)
    c: Coincident(g1,g2)
    c: Coincident(g2,g3)
    c: Coincident(g3,g0)
    c: Vertical(g0)
    c: Vertical(g2)
    c: Horizontal(g1)
    c: Horizontal(g3)
    c: Distance(g0,g2) = 22
    c: Distance(g1,g3) = 3
    c: Distance(g-1,g1) = 22
    c: Distance(g-2,g2) = 10.96
FEATURE [PartDesign::Pad] Pad006
  BaseFeature = -> Hole002
  Direction = (0,0,-1)
  Length = 41
  Length2 = 10
  Placement = pos=(7.86,7.86,9.485) rot=(0,0,1;0rad)
  Profile = -> Sketch009
  ReferenceAxis = -> Sketch009 [N_Axis]
  Refine = true
  SideType = 0
  Suppressed = false
  Type = 0
  Type2 = 0
FEATURE [Sketcher::SketchObject] Sketch010
  ArcFitTolerance = 1e-06
  AttachmentSupport = -> [Pad006]
  ExternalTypes = [0]
  FullyConstrained = true
  MakeInternals = false
  MapMode = 5
  Placement = pos=(7.86,7.86,-12.165) rot=(1,0,0;3.14159rad)
  _ExternalGeoVersion = 1
  sketch-geometry (4):
    g0: LineSegment StartX=11.04 StartY=-25 StartZ=0 EndX=11.04 EndY=-3.6e-15 EndZ=0
    g1: LineSegment StartX=-10.96 StartY=3.4e-15 StartZ=0 EndX=-10.96 EndY=-25 EndZ=0
    g2: LineSegment StartX=-10.96 StartY=-25 StartZ=0 EndX=11.04 EndY=-25 EndZ=0
    g3: ArcOfCircle CenterX=0.04 CenterY=2.91144e-05 CenterZ=0 NormalX=0 NormalY=0 NormalZ=1 AngleXU=0 Radius=11 StartAngle=6.28318 EndAngle=9.42478
  constraints (13):
    c: Coincident(g1,g2)
    c: Coincident(g2,g0)
    c: Vertical(g0)
    c: Vertical(g1)
    c: Horizontal(g2)
    c: Distance(g0,g1) = 22
    c: Distance(g0,g2) = 25
    c: Distance(g-1,g2) = 25
    c: Distance(g-2,g1) = 10.96
    c: Coincident(g3,g0)
    c: Radius(g3) = 11
    c: Equal(g1,g0)
    c: Coincident(g3,g1)
FEATURE [PartDesign::Pad] Pad007
  BaseFeature = -> Pad006
  Direction = (0,0,-1)
  Length = 3
  Length2 = 10
  Placement = pos=(7.86,7.86,9.485) rot=(0,0,1;0rad)
  Profile = -> Sketch010
  ReferenceAxis = -> Sketch010 [N_Axis]
  Refine = true
  SideType = 0
  Suppressed = false
  Type = 0
  Type2 = 0
FEATURE [Sketcher::SketchObject] Sketch011
  ArcFitTolerance = 1e-06
  AttachmentSupport = -> [Pad007]
  ExternalTypes = [0]
  FullyConstrained = true
  MakeInternals = false
  MapMode = 5
  Placement = pos=(7.86,7.86,-15.165) rot=(1,0,0;3.14159rad)
  _ExternalGeoVersion = 1
  sketch-geometry (1):
    g0: Circle CenterX=0 CenterY=7.8 CenterZ=0 NormalX=0 NormalY=0 NormalZ=1 AngleXU=0 Radius=1
  constraints (3):
    c: Diameter(g0) = 2
    c: PointOnObject(g0,g-2)
    c: Distance(g0,g-1) = 7.8
FEATURE [PartDesign::Hole] Hole003
  BaseFeature = -> Pad007
  BaseProfileType = 7
  CustomThreadClearance = 0
  Depth = 3
  DepthType = 0
  Diameter = 2.552
  DrillForDepth = false
  DrillPoint = 1
  DrillPointAngle = 118
  HoleCutCountersinkAngle = 90
  HoleCutCustomValues = false
  HoleCutDepth = 0
  HoleCutDiameter = 0
  HoleCutType = 0
  ModelThread = false
  Placement = pos=(7.86,7.86,9.485) rot=(0,0,1;0rad)
  Profile = -> Sketch011
  Refine = true
  Suppressed = false
  Tapered = false
  TaperedAngle = 90
  ThreadClass = 0
  ThreadDepth = 3
  ThreadDepthType = 0
  ThreadDiameter = 2.2
  ThreadDirection = 0
  ThreadFit = 2
  ThreadSize = 7
  ThreadType = 1
  Threaded = false
  UseCustomThreadClearance = false
FEATURE [PartDesign::PolarPattern] PolarPattern001
  Angle = 360
  Axis = -> Sketch011 [N_Axis]
  BaseFeature = -> Hole003
  Mode = 0
  Occurrences = 8
  Offset = 120
  Originals = -> [Hole003]
  Placement = pos=(7.86,7.86,9.485) rot=(0,0,1;0rad)
  Refine = true
  SpacingPattern = [0]
  Spacings = [-1,-1,-1,-1,-1,-1,-1]
  Suppressed = false
  TransformMode = 0
FEATURE [Sketcher::SketchObject] Sketch012
  ArcFitTolerance = 1e-06
  AttachmentSupport = -> [PolarPattern001]
  ExternalTypes = [0]
  FullyConstrained = true
  MakeInternals = false
  MapMode = 5
  Placement = pos=(7.86,7.86,-15.165) rot=(1,0,0;3.14159rad)
  _ExternalGeoVersion = 1
  sketch-geometry (1):
    g0: Circle CenterX=0 CenterY=0 CenterZ=0 NormalX=0 NormalY=0 NormalZ=1 AngleXU=0 Radius=4
  constraints (2):
    c: Diameter(g0) = 8
    c: Coincident(g0,g-1)
FEATURE [PartDesign::Hole] Hole004
  BaseFeature = -> PolarPattern001
  BaseProfileType = 7
  CustomThreadClearance = 0
  Depth = 3
  DepthType = 0
  Diameter = 6
  DrillForDepth = false
  DrillPoint = 1
  DrillPointAngle = 118
  HoleCutCountersinkAngle = 90
  HoleCutCustomValues = false
  HoleCutDepth = 0
  HoleCutDiameter = 0
  HoleCutType = 0
  ModelThread = false
  Placement = pos=(7.86,7.86,9.485) rot=(0,0,1;0rad)
  Profile = -> Sketch012
  Refine = true
  Suppressed = false
  Tapered = false
  TaperedAngle = 90
  ThreadClass = 0
  ThreadDepth = 3
  ThreadDepthType = 0
  ThreadDiameter = 6
  ThreadDirection = 0
  ThreadFit = 0
  ThreadSize = 0
  ThreadType = 0
  Threaded = false
  UseCustomThreadClearance = false
FEATURE [App::Point] Origin010  label="Origin012"
  Role = Origin
FEATURE [Sketcher::SketchObject] Sketch014
  ArcFitTolerance = 1e-06
  AttachmentSupport = -> [Hole004]
  ExternalTypes = [0]
  FullyConstrained = true
  MakeInternals = false
  MapMode = 5
  Placement = pos=(7.86,32.86,9.485) rot=(0,0.707107,0.707107;3.14159rad)
  _ExternalGeoVersion = 1
  sketch-geometry (1):
    g0: Circle CenterX=0 CenterY=6 CenterZ=0 NormalX=0 NormalY=0 NormalZ=1 AngleXU=0 Radius=1.1
  constraints (3):
    c: Diameter(g0) = 2.2
    c: PointOnObject(g0,g-2)
    c: Distance(g0,g-1) = 6
FEATURE [PartDesign::Hole] Hole005
  BaseFeature = -> Hole004
  BaseProfileType = 7
  CustomThreadClearance = 0
  Depth = 7
  DepthType = 0
  Diameter = 2.9
  DrillForDepth = false
  DrillPoint = 1
  DrillPointAngle = 118
  HoleCutCountersinkAngle = 90
  HoleCutCustomValues = false
  HoleCutDepth = 0
  HoleCutDiameter = 0
  HoleCutType = 0
  ModelThread = false
  Placement = pos=(7.86,7.86,9.485) rot=(0,0,1;0rad)
  Profile = -> Sketch014
  Refine = true
  Suppressed = false
  Tapered = false
  TaperedAngle = 90
  ThreadClass = 0
  ThreadDepth = 7
  ThreadDepthType = 0
  ThreadDiameter = 2.5
  ThreadDirection = 0
  ThreadFit = 0
  ThreadSize = 8
  ThreadType = 1
  Threaded = false
  UseCustomThreadClearance = false
FEATURE [PartDesign::PolarPattern] PolarPattern002
  Angle = 360
  Axis = -> Sketch014 [N_Axis]
  BaseFeature = -> Hole005
  Mode = 0
  Occurrences = 5
  Offset = 120
  Originals = -> [Hole005]
  Placement = pos=(7.86,7.86,9.485) rot=(0,0,1;0rad)
  Refine = true
  SpacingPattern = [0]
  Spacings = [-1,-1,-1,-1]
  Suppressed = false
  TransformMode = 0
FEATURE [PartDesign::Body] Body001
  AllowCompound = true
  Group = -> [CopyPart__Feature001,Sketch006,Pad005,Sketch007,Hole001,PolarPattern,Sketch008,Hole002,Sketch009,Pad006,Sketch010,Pad007,Sketch011,Hole003,PolarPattern001,Sketch012,Hole004,Sketch014,Hole005,PolarPattern002]
  Origin = -> Origin011
  Placement = pos=(4,-74,-8.5) rot=(0,0,1;0rad)
  Tip = -> PolarPattern002
FEATURE [PartDesign::Mirrored] Mirrored
  BaseFeature = -> Pad001
  MirrorPlane = -> Sketch001 [H_Axis]
  Originals = -> [Pad001]
  Refine = true
  Suppressed = false
  TransformMode = 0
FEATURE [Sketcher::SketchObject] Sketch015
  ArcFitTolerance = 1e-06
  AttachmentSupport = -> [Mirrored]
  ExternalTypes = [0]
  FullyConstrained = true
  MakeInternals = false
  MapMode = 5
  Placement = pos=(0,-33.5,-5.31e-14) rot=(0,0.707107,0.707107;3.14159rad)
  _ExternalGeoVersion = 1
  sketch-geometry (8):
    g0: LineSegment StartX=-69.58 StartY=-15.5 StartZ=0 EndX=-69.58 EndY=-19 EndZ=0
    g1: LineSegment StartX=-69.58 StartY=-19 StartZ=0 EndX=-63.28 EndY=-19 EndZ=0
    g2: LineSegment StartX=-63.28 StartY=-19 StartZ=0 EndX=-63.28 EndY=-15.5 EndZ=0
    g3: LineSegment StartX=-63.28 StartY=-15.5 StartZ=0 EndX=-69.58 EndY=-15.5 EndZ=0
    g4: LineSegment StartX=44.42 StartY=-15.5 StartZ=0 EndX=38.12 EndY=-15.5 EndZ=0
    g5: LineSegment StartX=38.12 StartY=-15.5 StartZ=0 EndX=38.12 EndY=-19 EndZ=0
    g6: LineSegment StartX=38.12 StartY=-19 StartZ=0 EndX=44.42 EndY=-19 EndZ=0
    g7: LineSegment StartX=44.42 StartY=-19 StartZ=0 EndX=44.42 EndY=-15.5 EndZ=0
  constraints (24):
    c: Coincident(g0,g1)
    c: Coincident(g1,g2)
    c: Coincident(g2,g3)
    c: Coincident(g3,g0)
    c: Vertical(g0)
    c: Vertical(g2)
    c: Horizontal(g1)
    c: Horizontal(g3)
    c: Distance(g0,g2) = 6.3
    c: Distance(g1,g3) = 3.5
    c: Coincident(g4,g5)
    c: Coincident(g5,g6)
    c: Coincident(g6,g7)
    c: Coincident(g7,g4)
    c: Horizontal(g4)
    c: Horizontal(g6)
    c: Vertical(g5)
    c: Vertical(g7)
    c: Distance(g-2,g7) = 44.42
    c: Distance(g6,g6) = 6.3
    c: Distance(g7,g7) = 3.5
    c: Distance(g-2,g0) = 69.58
    c: Distance(g-1,g1) = 19
    c: Distance(g-1,g6) = 19
FEATURE [PartDesign::Pad] Pad008
  BaseFeature = -> Mirrored
  Direction = (0,1,1.8e-15)
  Length = 23
  Length2 = 10
  Profile = -> Sketch015
  ReferenceAxis = -> Sketch015 [N_Axis]
  Refine = true
  SideType = 0
  Suppressed = false
  Type = 0
  Type2 = 0
FEATURE [PartDesign::Mirrored] Mirrored001
  BaseFeature = -> Pad008
  MirrorPlane = -> Sketch015 [H_Axis]
  Originals = -> [Pad008]
  Refine = true
  Suppressed = false
  TransformMode = 0
FEATURE [Sketcher::SketchObject] Sketch016
  ArcFitTolerance = 1e-06
  AttachmentSupport = -> [Mirrored001]
  ExternalGeometry = -> [Mirrored001]
  ExternalTypes = [0,0]
  FullyConstrained = true
  MakeInternals = false
  MapMode = 5
  Placement = pos=(0,-1.18e-14,-19) rot=(1,0,0;3.14159rad)
  _ExternalGeoVersion = 1
  sketch-geometry (12):
    g0: Circle CenterX=-35.52 CenterY=36 CenterZ=0 NormalX=0 NormalY=0 NormalZ=1 AngleXU=0 Radius=1.25
    g1: Circle CenterX=-27.52 CenterY=36 CenterZ=0 NormalX=0 NormalY=0 NormalZ=1 AngleXU=0 Radius=1.25
    g2: Circle CenterX=-19.52 CenterY=36 CenterZ=0 NormalX=0 NormalY=0 NormalZ=1 AngleXU=0 Radius=1.25
    g3: Circle CenterX=-11.52 CenterY=36 CenterZ=0 NormalX=0 NormalY=0 NormalZ=1 AngleXU=0 Radius=1.25
    g4: Circle CenterX=60.48 CenterY=36 CenterZ=0 NormalX=0 NormalY=0 NormalZ=1 AngleXU=0 Radius=1.25
    g5: Circle CenterX=52.48 CenterY=36 CenterZ=0 NormalX=0 NormalY=0 NormalZ=1 AngleXU=0 Radius=1.25
    g6: Circle CenterX=44.48 CenterY=36 CenterZ=0 NormalX=0 NormalY=0 NormalZ=1 AngleXU=0 Radius=1.25
    g7: Circle CenterX=36.48 CenterY=36 CenterZ=0 NormalX=0 NormalY=0 NormalZ=1 AngleXU=0 Radius=1.25
    g8: Circle CenterX=-41.02 CenterY=30.5 CenterZ=0 NormalX=0 NormalY=0 NormalZ=1 AngleXU=0 Radius=1.25
    g9: Circle CenterX=-41.02 CenterY=14.5 CenterZ=0 NormalX=0 NormalY=0 NormalZ=1 AngleXU=0 Radius=1.25
    g10: Circle CenterX=65.98 CenterY=30.5 CenterZ=0 NormalX=0 NormalY=0 NormalZ=1 AngleXU=0 Radius=1.25
    g11: Circle CenterX=65.98 CenterY=14.5 CenterZ=0 NormalX=0 NormalY=0 NormalZ=1 AngleXU=0 Radius=1.25
  constraints (36):
    c: Diameter(g0) = 2.5
    c: Distance(g0,g-1) = 36
    c: Equal(g1,g0)
    c: Equal(g2,g1)
    c: Equal(g3,g2)
    c: Distance(g1,g-1) = 36
    c: Distance(g2,g-1) = 36
    c: Distance(g3,g-1) = 36
    c: Distance(g0,g1) = 8
    c: Distance(g1,g2) = 8
    c: Distance(g2,g3) = 8
    c: Equal(g3,g7)
    c: Equal(g7,g6)
    c: Equal(g6,g5)
    c: Equal(g5,g4)
    c: Distance(g4,g-3) = 9.1
    c: Distance(g4,g-1) = 36
    c: Distance(g5,g-1) = 36
    c: Distance(g6,g-1) = 36
    c: Distance(g7,g-1) = 36
    c: Distance(g4,g5) = 8
    c: Distance(g5,g6) = 8
    c: Distance(g7,g6) = 8
    c: Diameter(g8) = 2.5
    c: Distance(g8,g-1) = 30.5
    c: Equal(g9,g8)
    c: Distance(g9,g8) = 16
    c: Equal(g10,g4)
    c: Distance(g10,g-3) = 3.6
    c: Distance(g10,g-1) = 30.5
    c: Equal(g11,g10)
    c: DistanceY(g11,g10) = 16
    c: Distance(g11,g-3) = 3.6
    c: Distance(g8,g-4) = 3.4
    c: Distance(g9,g-4) = 3.4
    c: Distance(g0,g-4) = 8.9
FEATURE [PartDesign::Hole] Hole
  BaseFeature = -> Mirrored001
  BaseProfileType = 7
  CustomThreadClearance = 0
  Depth = 4
  DepthType = 0
  Diameter = 3.1
  DrillForDepth = false
  DrillPoint = 1
  DrillPointAngle = 118
  HoleCutCountersinkAngle = 90
  HoleCutCustomValues = false
  HoleCutDepth = 0
  HoleCutDiameter = 0
  HoleCutType = 0
  ModelThread = false
  Profile = -> Sketch016
  Refine = true
  Suppressed = false
  Tapered = false
  TaperedAngle = 90
  ThreadClass = 0
  ThreadDepth = 4
  ThreadDepthType = 0
  ThreadDiameter = 2.5
  ThreadDirection = 0
  ThreadFit = 2
  ThreadSize = 8
  ThreadType = 1
  Threaded = false
  UseCustomThreadClearance = false
FEATURE [PartDesign::Mirrored] Mirrored002
  BaseFeature = -> Hole
  MirrorPlane = -> XY_Plane002
  Originals = -> [Hole]
  Refine = true
  Suppressed = false
  TransformMode = 0
FEATURE [PartDesign::ShapeBinder] CopyPart__Feature009
  Placement = pos=(0,0,19.16) rot=(0,0,1;1.5708rad)
  TraceSupport = false
FEATURE [App::Point] Origin013  label="Origin015"
  Role = Origin
FEATURE [Sketcher::SketchObject] Sketch018
  ArcFitTolerance = 1e-06
  AttachmentSupport = -> [CopyPart__Feature009]
  ExternalTypes = [0]
  FullyConstrained = true
  MakeInternals = false
  MapMode = 5
  Placement = pos=(0,0,21) rot=(0,0,1;1.5708rad)
  _ExternalGeoVersion = 1
  sketch-geometry (7):
    g0: ArcOfCircle CenterX=0.0210204 CenterY=-0.0225888 CenterZ=0 NormalX=0 NormalY=0 NormalZ=1 AngleXU=0 Radius=11 StartAngle=2.28533 EndAngle=5.42692
    g1: LineSegment StartX=7.22894 StartY=-8.33198 StartZ=0 EndX=17.8355 EndY=2.27462 EndZ=0
    g2: LineSegment StartX=-7.1869 StartY=8.2868 StartZ=0 EndX=14.0263 EndY=29.5 EndZ=0
    g3: LineSegment StartX=17.8355 StartY=2.27462 StartZ=0 EndX=22.1963 EndY=-14 EndZ=0
    g4: LineSegment StartX=22.1963 StartY=-14 StartZ=0 EndX=32.1963 EndY=-14 EndZ=0
    g5: LineSegment StartX=32.1963 StartY=-14 StartZ=0 EndX=32.1963 EndY=29.5 EndZ=0
    g6: LineSegment StartX=14.0263 StartY=29.5 StartZ=0 EndX=32.1963 EndY=29.5 EndZ=0
  constraints (22):
    c: Distance(g0,g0) = 22
    c: Angle(g0) = 3.14159
    c: Distance(g1) = 15
    c: Angle(g-1,g1) = 0.785398
    c: Coincident(g1,g0)
    c: Distance(g2) = 30
    c: Angle(g-1,g2) = 0.785398
    c: Coincident(g2,g0)
    c: Angle(g-1,g3) = -1.309
    c: Coincident(g3,g1)
    c: Coincident(g4,g3)
    c: Horizontal(g4)
    c: Coincident(g5,g4)
    c: Vertical(g5)
    c: Coincident(g6,g2)
    c: Coincident(g6,g5)
    c: Horizontal(g6)
    c: DistanceY(g5,g5) = 43.5
    c: Distance(g1,g-1) = 17.98
    c: Distance(g-1,g6) = 29.5
    c: Distance(g4,g4) = 10
    c: DistanceX(g6,g6) = 18.17
FEATURE [PartDesign::Pad] Pad009
  Direction = (0,0,1)
  Length = 5
  Length2 = 10
  Placement = pos=(0,0,19.16) rot=(0,0,1;1.5708rad)
  Profile = -> Sketch018
  ReferenceAxis = -> Sketch018 [N_Axis]
  Refine = true
  SideType = 0
  Suppressed = false
  Type = 0
  Type2 = 0
FEATURE [Sketcher::SketchObject] Sketch002
  ArcFitTolerance = 1e-06
  ExternalTypes = [0]
  FullyConstrained = true
  MakeInternals = false
  MapMode = 5
  Placement = pos=(0,0,26) rot=(0,0,1;1.5708rad)
  _ExternalGeoVersion = 1
  sketch-geometry (1):
    g0: Circle CenterX=0 CenterY=0 CenterZ=0 NormalX=0 NormalY=0 NormalZ=1 AngleXU=0 Radius=3
  constraints (2):
    c: Diameter(g0) = 6
    c: Coincident(g0,g-1)
FEATURE [PartDesign::Hole] Hole008
  BaseFeature = -> Pad009
  BaseProfileType = 7
  CustomThreadClearance = 0
  Depth = 5
  DepthType = 0
  Diameter = 7
  DrillForDepth = false
  DrillPoint = 1
  DrillPointAngle = 118
  HoleCutCountersinkAngle = 90
  HoleCutCustomValues = false
  HoleCutDepth = 0
  HoleCutDiameter = 0
  HoleCutType = 0
  ModelThread = false
  Placement = pos=(0,0,19.16) rot=(0,0,1;1.5708rad)
  Profile = -> Sketch002
  Refine = true
  Suppressed = false
  Tapered = false
  TaperedAngle = 90
  ThreadClass = 0
  ThreadDepth = 5
  ThreadDepthType = 0
  ThreadDiameter = 6
  ThreadDirection = 0
  ThreadFit = 2
  ThreadSize = 14
  ThreadType = 1
  Threaded = false
  UseCustomThreadClearance = false
FEATURE [Sketcher::SketchObject] Sketch019
  ArcFitTolerance = 1e-06
  ExternalTypes = [0]
  FullyConstrained = true
  MakeInternals = false
  MapMode = 5
  Placement = pos=(0,0,26) rot=(0,0,1;1.5708rad)
  _ExternalGeoVersion = 1
  sketch-geometry (1):
    g0: Circle CenterX=-8 CenterY=0 CenterZ=0 NormalX=0 NormalY=0 NormalZ=1 AngleXU=0 Radius=1.1
  constraints (3):
    c: Diameter(g0) = 2.2
    c: PointOnObject(g0,g-1)
    c: Distance(g0,g-2) = 8
FEATURE [PartDesign::Hole] Hole009
  BaseFeature = -> Hole008
  BaseProfileType = 7
  CustomThreadClearance = 0
  Depth = 5
  DepthType = 0
  Diameter = 3.1
  DrillForDepth = false
  DrillPoint = 0
  DrillPointAngle = 118
  HoleCutCountersinkAngle = 90
  HoleCutCustomValues = false
  HoleCutDepth = 0
  HoleCutDiameter = 0
  HoleCutType = 0
  ModelThread = false
  Placement = pos=(0,0,19.16) rot=(0,0,1;1.5708rad)
  Profile = -> Sketch019
  Refine = true
  Suppressed = false
  Tapered = false
  TaperedAngle = 90
  ThreadClass = 0
  ThreadDepth = 5
  ThreadDepthType = 0
  ThreadDiameter = 2.5
  ThreadDirection = 0
  ThreadFit = 2
  ThreadSize = 8
  ThreadType = 1
  Threaded = false
  UseCustomThreadClearance = false
FEATURE [PartDesign::PolarPattern] PolarPattern003
  Angle = 360
  Axis = -> Sketch019 [N_Axis]
  BaseFeature = -> Hole009
  Mode = 0
  Occurrences = 4
  Offset = 120
  Originals = -> [Hole009]
  Placement = pos=(0,0,19.16) rot=(0,0,1;1.5708rad)
  Refine = true
  SpacingPattern = [0]
  Spacings = [-1,-1,-1]
  Suppressed = false
  TransformMode = 0
FEATURE [PartDesign::Fillet] Fillet001
  Base = -> PolarPattern003 [Edge29,Edge5,Edge8]
  BaseFeature = -> PolarPattern003
  Placement = pos=(0,0,19.16) rot=(0,0,1;1.5708rad)
  Radius = 5
  Refine = true
  SupportTransform = false
  Suppressed = false
  UseAllEdges = false
FEATURE [Sketcher::SketchObject] Sketch023
  ArcFitTolerance = 1e-06
  AttachmentSupport = -> [Fillet001]
  ExternalTypes = [0]
  FullyConstrained = true
  MakeInternals = false
  MapMode = 5
  Placement = pos=(14,-1.5e-15,19.16) rot=(0.57735,0.57735,0.57735;2.0944rad)
  _ExternalGeoVersion = 1
  sketch-geometry (4):
    g0: LineSegment StartX=18.2 StartY=-49 StartZ=0 EndX=36.2 EndY=-49 EndZ=0
    g1: LineSegment StartX=36.2 StartY=-49 StartZ=0 EndX=36.2 EndY=49 EndZ=0
    g2: LineSegment StartX=36.2 StartY=49 StartZ=0 EndX=18.2 EndY=49 EndZ=0
    g3: LineSegment StartX=18.2 StartY=49 StartZ=0 EndX=18.2 EndY=-49 EndZ=0
  constraints (12):
    c: Coincident(g0,g1)
    c: Coincident(g1,g2)
    c: Vertical(g1)
    c: Horizontal(g0)
    c: Horizontal(g2)
    c: Distance(g2,g1) = 18
    c: Distance(g0,g2) = 98
    c: Coincident(g3,g2)
    c: Coincident(g3,g0)
    c: Vertical(g3)
    c: Distance(g-1,g0) = 49
    c: Distance(g-2,g3) = 18.2
FEATURE [PartDesign::Pad] Pad011
  BaseFeature = -> Fillet001
  Direction = (1,0,0)
  Length = 3
  Length2 = 10
  Placement = pos=(0,0,19.16) rot=(0,0,1;1.5708rad)
  Profile = -> Sketch023
  ReferenceAxis = -> Sketch023 [N_Axis]
  Refine = true
  SideType = 0
  Suppressed = false
  Type = 0
  Type2 = 0
FEATURE [PartDesign::ShapeBinder] CopyPart__Feature010
  Placement = pos=(0,0,19.16) rot=(0,0,1;1.5708rad)
  TraceSupport = false
FEATURE [App::Point] Origin015  label="Origin017"
  Role = Origin
FEATURE [Sketcher::SketchObject] Sketch024
  ArcFitTolerance = 1e-06
  ExternalTypes = [0]
  FullyConstrained = true
  MakeInternals = false
  MapMode = 5
  Placement = pos=(0,0,26) rot=(0,0,1;1.5708rad)
  _ExternalGeoVersion = 1
  sketch-geometry (1):
    g0: Circle CenterX=0 CenterY=0 CenterZ=0 NormalX=0 NormalY=0 NormalZ=1 AngleXU=0 Radius=3
  constraints (2):
    c: Diameter(g0) = 6
    c: Coincident(g0,g-1)
FEATURE [Sketcher::SketchObject] Sketch025
  ArcFitTolerance = 1e-06
  AttachmentSupport = -> [CopyPart__Feature010]
  ExternalTypes = [0]
  FullyConstrained = true
  MakeInternals = false
  MapMode = 5
  Placement = pos=(0,0,21) rot=(0,0,1;1.5708rad)
  _ExternalGeoVersion = 1
  sketch-geometry (7):
    g0: ArcOfCircle CenterX=0.0210204 CenterY=-0.0225888 CenterZ=0 NormalX=0 NormalY=0 NormalZ=1 AngleXU=0 Radius=11 StartAngle=2.28533 EndAngle=5.42692
    g1: LineSegment StartX=7.22894 StartY=-8.33198 StartZ=0 EndX=17.8355 EndY=2.27462 EndZ=0
    g2: LineSegment StartX=-7.1869 StartY=8.2868 StartZ=0 EndX=14.0263 EndY=29.5 EndZ=0
    g3: LineSegment StartX=17.8355 StartY=2.27462 StartZ=0 EndX=22.1963 EndY=-14 EndZ=0
    g4: LineSegment StartX=22.1963 StartY=-14 StartZ=0 EndX=32.1963 EndY=-14 EndZ=0
    g5: LineSegment StartX=32.1963 StartY=-14 StartZ=0 EndX=32.1963 EndY=29.5 EndZ=0
    g6: LineSegment StartX=14.0263 StartY=29.5 StartZ=0 EndX=32.1963 EndY=29.5 EndZ=0
  constraints (22):
    c: Distance(g0,g0) = 22
    c: Angle(g0) = 3.14159
    c: Distance(g1) = 15
    c: Angle(g-1,g1) = 0.785398
    c: Coincident(g1,g0)
    c: Distance(g2) = 30
    c: Angle(g-1,g2) = 0.785398
    c: Coincident(g2,g0)
    c: Angle(g-1,g3) = -1.309
    c: Coincident(g3,g1)
    c: Coincident(g4,g3)
    c: Horizontal(g4)
    c: Coincident(g5,g4)
    c: Vertical(g5)
    c: Coincident(g6,g2)
    c: Coincident(g6,g5)
    c: Horizontal(g6)
    c: DistanceY(g5,g5) = 43.5
    c: Distance(g1,g-1) = 17.98
    c: Distance(g-1,g6) = 29.5
    c: Distance(g4,g4) = 10
    c: DistanceX(g6,g6) = 18.17
FEATURE [PartDesign::Pad] Pad012
  Direction = (0,0,1)
  Length = 5
  Length2 = 10
  Placement = pos=(0,0,19.16) rot=(0,0,1;1.5708rad)
  Profile = -> Sketch025
  ReferenceAxis = -> Sketch025 [N_Axis]
  Refine = true
  SideType = 0
  Suppressed = false
  Type = 0
  Type2 = 0
FEATURE [PartDesign::Hole] Hole010
  BaseFeature = -> Pad012
  BaseProfileType = 7
  CustomThreadClearance = 0
  Depth = 5
  DepthType = 0
  Diameter = 7
  DrillForDepth = false
  DrillPoint = 1
  DrillPointAngle = 118
  HoleCutCountersinkAngle = 90
  HoleCutCustomValues = false
  HoleCutDepth = 0
  HoleCutDiameter = 0
  HoleCutType = 0
  ModelThread = false
  Placement = pos=(0,0,19.16) rot=(0,0,1;1.5708rad)
  Profile = -> Sketch024
  Refine = true
  Suppressed = false
  Tapered = false
  TaperedAngle = 90
  ThreadClass = 0
  ThreadDepth = 5
  ThreadDepthType = 0
  ThreadDiameter = 6
  ThreadDirection = 0
  ThreadFit = 2
  ThreadSize = 14
  ThreadType = 1
  Threaded = false
  UseCustomThreadClearance = false
FEATURE [Sketcher::SketchObject] Sketch026
  ArcFitTolerance = 1e-06
  ExternalTypes = [0]
  FullyConstrained = true
  MakeInternals = false
  MapMode = 5
  Placement = pos=(0,0,26) rot=(0,0,1;1.5708rad)
  _ExternalGeoVersion = 1
  sketch-geometry (1):
    g0: Circle CenterX=-8 CenterY=0 CenterZ=0 NormalX=0 NormalY=0 NormalZ=1 AngleXU=0 Radius=1.1
  constraints (3):
    c: Diameter(g0) = 2.2
    c: PointOnObject(g0,g-1)
    c: Distance(g0,g-2) = 8
FEATURE [PartDesign::Hole] Hole011
  BaseFeature = -> Hole010
  BaseProfileType = 7
  CustomThreadClearance = 0
  Depth = 5
  DepthType = 0
  Diameter = 3.1
  DrillForDepth = false
  DrillPoint = 0
  DrillPointAngle = 118
  HoleCutCountersinkAngle = 90
  HoleCutCustomValues = false
  HoleCutDepth = 0
  HoleCutDiameter = 0
  HoleCutType = 0
  ModelThread = false
  Placement = pos=(0,0,19.16) rot=(0,0,1;1.5708rad)
  Profile = -> Sketch026
  Refine = true
  Suppressed = false
  Tapered = false
  TaperedAngle = 90
  ThreadClass = 0
  ThreadDepth = 5
  ThreadDepthType = 0
  ThreadDiameter = 2.5
  ThreadDirection = 0
  ThreadFit = 2
  ThreadSize = 8
  ThreadType = 1
  Threaded = false
  UseCustomThreadClearance = false
FEATURE [PartDesign::PolarPattern] PolarPattern004
  Angle = 360
  Axis = -> Sketch026 [N_Axis]
  BaseFeature = -> Hole011
  Mode = 0
  Occurrences = 4
  Offset = 120
  Originals = -> [Hole011]
  Placement = pos=(0,0,19.16) rot=(0,0,1;1.5708rad)
  Refine = true
  SpacingPattern = [0]
  Spacings = [-1,-1,-1]
  Suppressed = false
  TransformMode = 0
FEATURE [PartDesign::Fillet] Fillet002
  Base = -> PolarPattern004 [Edge29,Edge5,Edge8]
  BaseFeature = -> PolarPattern004
  Placement = pos=(0,0,19.16) rot=(0,0,1;1.5708rad)
  Radius = 5
  Refine = true
  SupportTransform = false
  Suppressed = false
  UseAllEdges = false
FEATURE [Sketcher::SketchObject] Sketch027
  ArcFitTolerance = 1e-06
  AttachmentSupport = -> [Fillet002]
  ExternalTypes = [0]
  FullyConstrained = true
  MakeInternals = false
  MapMode = 5
  Placement = pos=(14,-1.5e-15,19.16) rot=(0.57735,0.57735,0.57735;2.0944rad)
  _ExternalGeoVersion = 1
  sketch-geometry (4):
    g0: LineSegment StartX=17.2 StartY=-41.25 StartZ=0 EndX=37.2 EndY=-41.25 EndZ=0
    g1: LineSegment StartX=37.2 StartY=-41.25 StartZ=0 EndX=37.2 EndY=58.75 EndZ=0
    g2: LineSegment StartX=37.2 StartY=58.75 StartZ=0 EndX=17.2 EndY=58.75 EndZ=0
    g3: LineSegment StartX=17.2 StartY=58.75 StartZ=0 EndX=17.2 EndY=-41.25 EndZ=0
  constraints (12):
    c: Coincident(g0,g1)
    c: Coincident(g1,g2)
    c: Vertical(g1)
    c: Horizontal(g0)
    c: Horizontal(g2)
    c: Distance(g2,g1) = 20
    c: Distance(g0,g2) = 100
    c: Coincident(g3,g2)
    c: Coincident(g3,g0)
    c: Vertical(g3)
    c: Distance(g-1,g0) = 41.25
    c: Distance(g-2,g3) = 17.2
FEATURE [PartDesign::Pad] Pad013
  BaseFeature = -> Fillet002
  Direction = (1,0,0)
  Length = 3
  Length2 = 10
  Placement = pos=(0,0,19.16) rot=(0,0,1;1.5708rad)
  Profile = -> Sketch027
  ReferenceAxis = -> Sketch027 [N_Axis]
  Refine = true
  SideType = 0
  Suppressed = false
  Type = 0
  Type2 = 0
FEATURE [Sketcher::SketchObject] Sketch028
  ArcFitTolerance = 1e-06
  AttachmentSupport = -> [Pad013]
  ExternalTypes = [0]
  FullyConstrained = true
  MakeInternals = false
  MapMode = 5
  Placement = pos=(-1.9e-15,17.2,19.16) rot=(1,0,0;1.5708rad)
  _ExternalGeoVersion = 1
  sketch-geometry (4):
    g0: LineSegment StartX=14 StartY=-41.25 StartZ=0 EndX=19 EndY=-41.25 EndZ=0
    g1: LineSegment StartX=19 StartY=-41.25 StartZ=0 EndX=19 EndY=58.75 EndZ=0
    g2: LineSegment StartX=19 StartY=58.75 StartZ=0 EndX=14 EndY=58.75 EndZ=0
    g3: LineSegment StartX=14 StartY=58.75 StartZ=0 EndX=14 EndY=-41.25 EndZ=0
  constraints (12):
    c: Coincident(g0,g1)
    c: Coincident(g1,g2)
    c: Vertical(g1)
    c: Horizontal(g0)
    c: Horizontal(g2)
    c: Distance(g2,g1) = 5
    c: Distance(g0,g2) = 100
    c: Coincident(g3,g2)
    c: Coincident(g3,g0)
    c: Vertical(g3)
    c: Distance(g-2,g3) = 14
    c: Distance(g-1,g2) = 58.75
FEATURE [PartDesign::Pad] Pad014
  BaseFeature = -> Pad013
  Direction = (0,-1,2e-16)
  Length = 2
  Length2 = 10
  Placement = pos=(0,0,19.16) rot=(0,0,1;1.5708rad)
  Profile = -> Sketch028
  ReferenceAxis = -> Sketch028 [N_Axis]
  Refine = true
  SideType = 0
  Suppressed = false
  Type = 0
  Type2 = 0
FEATURE [Sketcher::SketchObject] Sketch029
  ArcFitTolerance = 1e-06
  AttachmentSupport = -> [Pad014]
  ExternalTypes = [0]
  FullyConstrained = true
  MakeInternals = false
  MapMode = 5
  Placement = pos=(-2.11e-14,0,77.91) rot=(0,0,1;1.5708rad)
  _ExternalGeoVersion = 1
  sketch-geometry (4):
    g0: LineSegment StartX=15.2 StartY=-14 StartZ=0 EndX=15.2 EndY=-19 EndZ=0
    g1: LineSegment StartX=15.2 StartY=-19 StartZ=0 EndX=37.2 EndY=-19 EndZ=0
    g2: LineSegment StartX=37.2 StartY=-19 StartZ=0 EndX=37.2 EndY=-14 EndZ=0
    g3: LineSegment StartX=37.2 StartY=-14 StartZ=0 EndX=15.2 EndY=-14 EndZ=0
  constraints (12):
    c: Coincident(g0,g1)
    c: Coincident(g1,g2)
    c: Horizontal(g1)
    c: Vertical(g0)
    c: Vertical(g2)
    c: Distance(g0,g2) = 22
    c: Distance(g2,g1) = 5
    c: Coincident(g3,g2)
    c: Coincident(g3,g0)
    c: Horizontal(g3)
    c: Distance(g-2,g0) = 15.2
    c: Distance(g-1,g1) = 19
FEATURE [PartDesign::Pad] Pad015
  BaseFeature = -> Pad014
  Direction = (0,0,1)
  Length = 2
  Length2 = 10
  Placement = pos=(0,0,19.16) rot=(0,0,1;1.5708rad)
  Profile = -> Sketch029
  ReferenceAxis = -> Sketch029 [N_Axis]
  Refine = true
  SideType = 0
  Suppressed = false
  Type = 0
  Type2 = 0
FEATURE [Sketcher::SketchObject] Sketch030
  ArcFitTolerance = 1e-06
  AttachmentSupport = -> [Pad015]
  ExternalTypes = [0]
  FullyConstrained = true
  MakeInternals = false
  MapMode = 5
  Placement = pos=(1.49e-14,0,-22.09) rot=(0.707107,0.707107,0;3.14159rad)
  _ExternalGeoVersion = 1
  sketch-geometry (4):
    g0: LineSegment StartX=37.2 StartY=14 StartZ=0 EndX=37.2 EndY=19 EndZ=0
    g1: LineSegment StartX=37.2 StartY=19 StartZ=0 EndX=15.2 EndY=19 EndZ=0
    g2: LineSegment StartX=15.2 StartY=19 StartZ=0 EndX=15.2 EndY=14 EndZ=0
    g3: LineSegment StartX=37.2 StartY=14 StartZ=0 EndX=15.2 EndY=14 EndZ=0
  constraints (12):
    c: Coincident(g0,g1)
    c: Coincident(g1,g2)
    c: Vertical(g0)
    c: Vertical(g2)
    c: Horizontal(g1)
    c: Distance(g0,g2) = 22
    c: Distance(g1,g0) = 5
    c: Coincident(g3,g0)
    c: Coincident(g3,g2)
    c: Horizontal(g3)
    c: Distance(g-2,g2) = 15.2
    c: Distance(g-1,g3) = 14
FEATURE [PartDesign::Pad] Pad016
  BaseFeature = -> Pad015
  Direction = (0,0,-1)
  Length = 2
  Length2 = 10
  Placement = pos=(0,0,19.16) rot=(0,0,1;1.5708rad)
  Profile = -> Sketch030
  ReferenceAxis = -> Sketch030 [N_Axis]
  Refine = true
  SideType = 0
  Suppressed = false
  Type = 0
  Type2 = 0
FEATURE [PartDesign::Fillet] Fillet003
  Base = -> Pad011 [Edge13,Edge39,Edge29,Edge40]
  BaseFeature = -> Pad011
  Placement = pos=(0,0,19.16) rot=(0,0,1;1.5708rad)
  Radius = 3
  Refine = true
  SupportTransform = false
  Suppressed = false
  UseAllEdges = false
FEATURE [PartDesign::Fillet] Fillet004
  Base = -> Pad016 [Edge25,Edge28,Edge26,Edge27]
  BaseFeature = -> Pad016
  Placement = pos=(0,0,19.16) rot=(0,0,1;1.5708rad)
  Radius = 4
  Refine = true
  SupportTransform = false
  Suppressed = false
  UseAllEdges = false
FEATURE [PartDesign::Body] Body003
  AllowCompound = true
  Group = -> [CopyPart__Feature010,Sketch025,Pad012,Sketch024,Hole010,Sketch026,Hole011,PolarPattern004,Fillet002,Sketch027,Pad013,Sketch028,Pad014,Sketch029,Pad015,Sketch030,Pad016,Fillet004]
  Origin = -> Origin014
  Placement = pos=(30,-22,47) rot=(0,1,0;3.14159rad)
  Tip = -> Fillet004
FEATURE [Part::Feature] Part__Feature022  label="Body008"
  Placement = pos=(-5,-22,0) rot=(0,0,1;0rad)
  shape: bbox 23 x 46 x 30 mm, 41 faces (baked)
FEATURE [Sketcher::SketchObject] Sketch031
  ArcFitTolerance = 1e-06
  AttachmentSupport = -> [Fillet003]
  ExternalTypes = [0,0]
  FullyConstrained = true
  MakeInternals = false
  MapMode = 5
  Placement = pos=(14,0,19.16) rot=(0.57735,-0.57735,-0.57735;2.0944rad)
  _ExternalGeoVersion = 1
  sketch-geometry (1):
    g0: Circle CenterX=-27.2 CenterY=15 CenterZ=0 NormalX=0 NormalY=0 NormalZ=1 AngleXU=0 Radius=2.5
  constraints (3):
    c: Distance(g0,g-2) = 27.2
    c: DistanceY(g-1,g0) = 15
    c: Diameter(g0) = 5
FEATURE [PartDesign::Pad] Pad017
  BaseFeature = -> Fillet003
  Direction = (-1,0,0)
  Length = 60
  Length2 = 10
  Placement = pos=(0,0,19.16) rot=(0,0,1;1.5708rad)
  Profile = -> Sketch031
  ReferenceAxis = -> Sketch031 [N_Axis]
  Refine = true
  SideType = 0
  Suppressed = false
  Type = 0
  Type2 = 0
FEATURE [PartDesign::Fillet] Fillet005
  Base = -> Pad017 [Face26]
  BaseFeature = -> Pad017
  Placement = pos=(0,0,19.16) rot=(0,0,1;1.5708rad)
  Radius = 2
  Refine = true
  SupportTransform = false
  Suppressed = false
  UseAllEdges = false
FEATURE [PartDesign::Body] Body002
  AllowCompound = true
  Group = -> [CopyPart__Feature009,Sketch018,Pad009,Sketch002,Hole008,Sketch019,Hole009,PolarPattern003,Fillet001,Sketch023,Pad011,Fillet003,Sketch031,Pad017,Fillet005]
  Origin = -> Origin012
  Placement = pos=(-5,-22,0) rot=(0,0,1;0rad)
  Tip = -> Fillet005
FEATURE [Sketcher::SketchObject] Sketch032
  ArcFitTolerance = 1e-06
  AttachmentSupport = -> [Mirrored002]
  ExternalTypes = [0]
  FullyConstrained = true
  MakeInternals = false
  MapMode = 5
  Placement = pos=(69.58,6.04e-14,0) rot=(0.57735,0.57735,0.57735;2.0944rad)
  _ExternalGeoVersion = 1
  sketch-geometry (10):
    g0: LineSegment StartX=-43.5 StartY=19 StartZ=0 EndX=-43.5 EndY=-19 EndZ=0
    g1: LineSegment StartX=-43.5 StartY=-19 StartZ=0 EndX=-10.5 EndY=-19 EndZ=0
    g2: LineSegment StartX=-10.5 StartY=-19 StartZ=0 EndX=-10.5 EndY=19 EndZ=0
    g3: LineSegment StartX=-43.5 StartY=19 StartZ=0 EndX=-10.5 EndY=19 EndZ=0
    g4: Circle CenterX=-35 CenterY=4 CenterZ=0 NormalX=0 NormalY=0 NormalZ=1 AngleXU=0 Radius=1.5
    g5: Circle CenterX=-35 CenterY=-4 CenterZ=0 NormalX=0 NormalY=0 NormalZ=1 AngleXU=0 Radius=1.5
    g6: Circle CenterX=-35 CenterY=-12 CenterZ=0 NormalX=0 NormalY=0 NormalZ=1 AngleXU=0 Radius=1.5
    g7: Circle CenterX=-35 CenterY=12 CenterZ=0 NormalX=0 NormalY=0 NormalZ=1 AngleXU=0 Radius=1.5
    g8: Circle CenterX=-28 CenterY=8 CenterZ=0 NormalX=0 NormalY=0 NormalZ=1 AngleXU=0 Radius=1.5
    g9: Circle CenterX=-28 CenterY=-8 CenterZ=0 NormalX=0 NormalY=0 NormalZ=1 AngleXU=0 Radius=1.5
  constraints (30):
    c: Coincident(g0,g1)
    c: Coincident(g1,g2)
    c: Vertical(g0)
    c: Vertical(g2)
    c: Horizontal(g1)
    c: Distance(g0,g2) = 33
    c: Distance(g1,g0) = 38
    c: Coincident(g3,g0)
    c: Coincident(g3,g2)
    c: Horizontal(g3)
    c: Distance(g-2,g2) = 10.5
    c: Distance(g-1,g3) = 19
    c: Diameter(g4) = 3
    c: Diameter(g5) = 3
    c: Diameter(g6) = 3
    c: Diameter(g7) = 3
    c: Distance(g7,g-2) = 35
    c: Distance(g4,g-2) = 35
    c: Distance(g5,g-2) = 35
    c: Distance(g6,g-2) = 35
    c: Distance(g7,g-1) = 12
    c: Distance(g7,g4) = 8
    c: Distance(g6,g-1) = 12
    c: Distance(g5,g6) = 8
    c: Diameter(g8) = 3
    c: Diameter(g9) = 3
    c: Distance(g8,g-1) = 8
    c: Distance(g9,g-1) = 8
    c: Distance(g8,g-2) = 28
    c: Distance(g9,g-2) = 28
FEATURE [PartDesign::Pad] Pad018
  BaseFeature = -> Mirrored002
  Direction = (1,0,0)
  Length = 2
  Length2 = 10
  Profile = -> Sketch032
  ReferenceAxis = -> Sketch032 [N_Axis]
  Refine = true
  SideType = 0
  Suppressed = false
  Type = 0
  Type2 = 0
FEATURE [Sketcher::SketchObject] Sketch033
  ArcFitTolerance = 1e-06
  AttachmentSupport = -> [Pad018]
  ExternalTypes = [0]
  FullyConstrained = true
  MakeInternals = false
  MapMode = 5
  Placement = pos=(71.58,0,0) rot=(0.57735,0.57735,0.57735;2.0944rad)
  _ExternalGeoVersion = 1
  sketch-geometry (1):
    g0: Circle CenterX=-15.5 CenterY=0 CenterZ=0 NormalX=0 NormalY=0 NormalZ=1 AngleXU=0 Radius=2.5
  constraints (3):
    c: Diameter(g0) = 5
    c: PointOnObject(g0,g-1)
    c: Distance(g0,g-1) = 15.5
FEATURE [PartDesign::Pad] Pad019
  BaseFeature = -> Pad018
  Direction = (1,0,0)
  Length = 7
  Length2 = 10
  Profile = -> Sketch033
  ReferenceAxis = -> Sketch033 [N_Axis]
  Refine = true
  SideType = 0
  Suppressed = false
  Type = 0
  Type2 = 0
FEATURE [PartDesign::Fillet] Fillet
  Base = -> Pad019 [Edge79]
  BaseFeature = -> Pad019
  Radius = 2
  Refine = true
  SupportTransform = false
  Suppressed = false
  UseAllEdges = false
FEATURE [PartDesign::Fillet] Fillet006
  Base = -> Fillet [Edge3,Edge4,Edge2,Edge14,Edge15,Edge22,Edge16,Edge35]
  BaseFeature = -> Fillet
  Radius = 2
  Refine = true
  SupportTransform = false
  Suppressed = false
  UseAllEdges = false
FEATURE [PartDesign::Body] Body
  AllowCompound = true
  Group = -> [CopyPart__Feature,Sketch,Pad,Sketch001,Pad001,Mirrored,Sketch015,Pad008,Mirrored001,Sketch016,Hole,Mirrored002,Sketch032,Pad018,Sketch033,Pad019,Fillet,Fillet006]
  Origin = -> Origin004
  Tip = -> Fillet006
